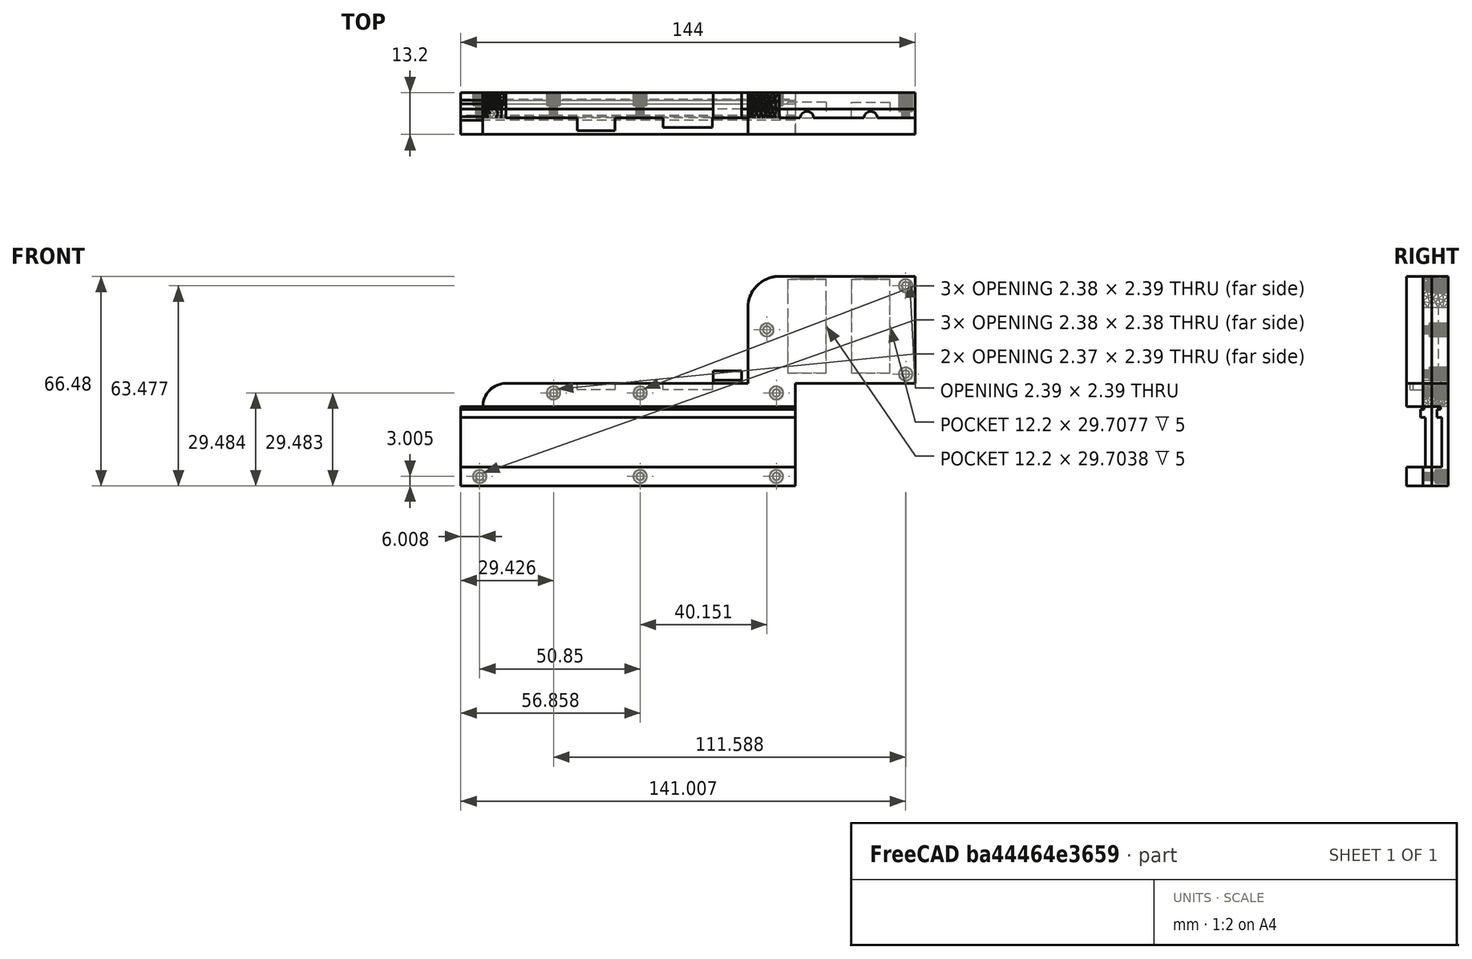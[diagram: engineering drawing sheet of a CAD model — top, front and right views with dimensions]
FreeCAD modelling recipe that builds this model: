
FCSTD DOCUMENT  (FreeCAD 0.19R24276 (Git))
Label: Feeder
License: All rights reserved
LicenseURL: http://en.wikipedia.org/wiki/All_rights_reserved
objects: Sketcher::SketchObject×7, Part::Feature×5, PartDesign::Pocket×3, Mesh::Feature×3, Part::Refine×2, PartDesign::Pad×1, PartDesign::Body×1
note: 23 computed .brp shape members not serialized (recipe doc carries the construction recipe); baked Part::Feature solids carry a one-line shape summary decoded from their .brp

FEATURE [Part::Feature] Feeder_8mm_Left_8mm_0_9_mm_tape001001_solid  label="Feeder_8mm_Left_8mm_0_9_mm_tape (Solid)"
  shape: bbox 144 x 12 x 66.48 mm, 7646 faces (baked)
FEATURE [Sketcher::SketchObject] Sketch  label="RightMain"
  FullyConstrained = false
  MapMode = 5
  Placement = pos=(0,0,0) rot=(1,0,0;1.5708rad)
  Support = -> [XZ_Plane]
  sketch-geometry (11):
    g0: LineSegment StartX=91 StartY=31.78 StartZ=0 EndX=91 EndY=7.78 EndZ=0
    g1: LineSegment StartX=144 StartY=41.78 StartZ=0 EndX=101 EndY=41.78 EndZ=0
    g2: LineSegment StartX=144 StartY=7.78 StartZ=0 EndX=144 EndY=41.78 EndZ=0
    g3: LineSegment StartX=106 StartY=7.78 StartZ=0 EndX=144 EndY=7.78 EndZ=0
    g4: LineSegment StartX=106 StartY=-24.7 StartZ=0 EndX=106 EndY=7.78 EndZ=0
    g5: LineSegment StartX=0 StartY=-24.7 StartZ=0 EndX=106 EndY=-24.7 EndZ=0
    g6: LineSegment StartX=0 StartY=0.4 StartZ=0 EndX=0 EndY=-24.7 EndZ=0
    g7: LineSegment StartX=7 StartY=0.4 StartZ=0 EndX=0 EndY=0.4 EndZ=0
    g8: LineSegment StartX=91 StartY=7.78 StartZ=0 EndX=14.38 EndY=7.78 EndZ=0
    g9: ArcOfCircle CenterX=14.401 CenterY=0.379003 CenterZ=0 NormalX=0 NormalY=0 NormalZ=1 AngleXU=0 Radius=7.40103 StartAngle=1.57363 EndAngle=3.13876
    g10: ArcOfCircle CenterX=101.048 CenterY=31.7317 CenterZ=0 NormalX=0 NormalY=0 NormalZ=1 AngleXU=0 Radius=10.0484 StartAngle=1.5756 EndAngle=3.13679
  constraints (23):
    c: Coincident(g1,g2)
    c: Vertical(g2)
    c: Coincident(g2,g3)
    c: Horizontal(g3)
    c: Coincident(g3,g4)
    c: Vertical(g4)
    c: Coincident(g4,g5)
    c: Horizontal(g5)
    c: Coincident(g5,g6)
    c: Coincident(g6,g7)
    c: Block(g8)
    c: Horizontal(g9,g8)
    c: Vertical(g9,g8)
    c: Block(g7)
    c: Horizontal(g9,g7)
    c: Vertical(g9,g7)
    c: Block(g1)
    c: Vertical(g10,g1)
    c: Horizontal(g10,g1)
    c: Block(g0)
    c: Horizontal(g0,g10)
    c: Vertical(g10,g0)
    c: DistanceX(g7,g7) = 7
FEATURE [Sketcher::SketchObject] Sketch001
  FullyConstrained = false
  Placement = pos=(0,0,0) rot=(1,0,0;1.5708rad)
  sketch-geometry (12):
    g0: LineSegment StartX=-41.78 StartY=5.2 StartZ=0 EndX=24.7 EndY=5.2 EndZ=0
    g1: LineSegment StartX=-41.78 StartY=-2.8 StartZ=0 EndX=-41.78 EndY=5.2 EndZ=0
    g2: LineSegment StartX=-0.4 StartY=-2.8 StartZ=0 EndX=-41.78 EndY=-2.8 EndZ=0
    g3: LineSegment StartX=-0.4 StartY=2.8 StartZ=0 EndX=-0.4 EndY=-2.8 EndZ=0
    g4: LineSegment StartX=0.5 StartY=2.8 StartZ=0 EndX=-0.4 EndY=2.8 EndZ=0
    g5: LineSegment StartX=0.5 StartY=1.7 StartZ=0 EndX=0.5 EndY=2.8 EndZ=0
    g6: LineSegment StartX=3 StartY=1.7 StartZ=0 EndX=0.5 EndY=1.7 EndZ=0
    g7: LineSegment StartX=3 StartY=3.2 StartZ=0 EndX=3 EndY=1.7 EndZ=0
    g8: LineSegment StartX=18.7 StartY=3.2 StartZ=0 EndX=3 EndY=3.2 EndZ=0
    g9: LineSegment StartX=18.7 StartY=-2.8 StartZ=0 EndX=18.7 EndY=3.2 EndZ=0
    g10: LineSegment StartX=24.7 StartY=-2.8 StartZ=0 EndX=18.7 EndY=-2.8 EndZ=0
    g11: LineSegment StartX=24.7 StartY=5.2 StartZ=0 EndX=24.7 EndY=-2.8 EndZ=0
  constraints (25):
    c: Horizontal(g0)
    c: Coincident(g0,g1)
    c: Vertical(g1)
    c: Coincident(g1,g2)
    c: Horizontal(g2)
    c: Coincident(g2,g3)
    c: Vertical(g3)
    c: Coincident(g3,g4)
    c: Horizontal(g4)
    c: Coincident(g4,g5)
    c: Vertical(g5)
    c: Coincident(g5,g6)
    c: Horizontal(g6)
    c: Coincident(g6,g7)
    c: Vertical(g7)
    c: Coincident(g7,g8)
    c: Horizontal(g8)
    c: Coincident(g8,g9)
    c: Vertical(g9)
    c: Coincident(g9,g10)
    c: Horizontal(g10)
    c: Coincident(g10,g11)
    c: Vertical(g11)
    c: Coincident(g11,g0)
    c: Block(g3)
FEATURE [PartDesign::Pad] Pad
  Direction = (1,1,1)
  Length = 8
  Length2 = 100
  Placement = pos=(0,0,0) rot=(1,0,0;1.5708rad)
  Profile = -> Sketch
  Type = 0
FEATURE [Sketcher::SketchObject] Sketch002  label="RightTapeHole"
  ExternalGeometry = -> [Pad]
  FullyConstrained = true
  MapMode = 5
  Placement = pos=(0,-8,-1.8e-15) rot=(1,0,0;1.5708rad)
  Support = -> [Pad]
  sketch-geometry (4):
    g0: LineSegment StartX=0 StartY=0.4 StartZ=0 EndX=106 EndY=0.4 EndZ=0
    g1: LineSegment StartX=106 StartY=0.4 StartZ=0 EndX=106 EndY=-0.5 EndZ=0
    g2: LineSegment StartX=106 StartY=-0.5 StartZ=0 EndX=0 EndY=-0.5 EndZ=0
    g3: LineSegment StartX=0 StartY=-0.5 StartZ=0 EndX=0 EndY=0.4 EndZ=0
  constraints (12):
    c: Coincident(g0,g1)
    c: Coincident(g1,g2)
    c: Coincident(g2,g3)
    c: Coincident(g3,g0)
    c: Horizontal(g0)
    c: Horizontal(g2)
    c: Vertical(g1)
    c: Vertical(g3)
    c: Horizontal(g-3,g0)
    c: Vertical(g0,g-3)
    c: Vertical(g0,g-4)
    c: DistanceY(g1,g1) = 0.9
FEATURE [PartDesign::Pocket] Pocket
  BaseFeature = -> Pad
  Length = 5.6
  Length2 = 100
  Placement = pos=(0,0,0) rot=(1,0,0;1.5708rad)
  Profile = -> Sketch002
  Type = 0
FEATURE [Sketcher::SketchObject] Sketch003  label="RightComponentHole1"
  ExternalGeometry = -> [Sketch]
  FullyConstrained = false
  MapMode = 5
  Placement = pos=(0,-8,-1.8e-15) rot=(1,0,0;1.5708rad)
  Support = -> [Pocket]
  sketch-geometry (4):
    g0: LineSegment StartX=0 StartY=0.4 StartZ=0 EndX=106 EndY=0.4 EndZ=0
    g1: LineSegment StartX=106 StartY=0.4 StartZ=0 EndX=106 EndY=-18.7 EndZ=0
    g2: LineSegment StartX=106 StartY=-18.7 StartZ=0 EndX=0 EndY=-18.7 EndZ=0
    g3: LineSegment StartX=0 StartY=-18.7 StartZ=0 EndX=0 EndY=0.4 EndZ=0
  constraints (11):
    c: Coincident(g0,g1)
    c: Coincident(g1,g2)
    c: Coincident(g2,g3)
    c: Coincident(g3,g0)
    c: Horizontal(g0)
    c: Horizontal(g2)
    c: Vertical(g3)
    c: Vertical(g0,g-3)
    c: DistanceY(g-5,g2) = 6
    c: Vertical(g1,g-5)
    c: Vertical(g0,g-4)
FEATURE [PartDesign::Pocket] Pocket001
  BaseFeature = -> Pocket
  Length = 4.5
  Length2 = 100
  Placement = pos=(0,0,0) rot=(1,0,0;1.5708rad)
  Profile = -> Sketch003
  Type = 0
FEATURE [Sketcher::SketchObject] Sketch004  label="RightComponentHole2"
  ExternalGeometry = -> [Sketch]
  FullyConstrained = true
  MapMode = 5
  Placement = pos=(0,-8,-1.8e-15) rot=(1,0,0;1.5708rad)
  Support = -> [Pad]
  sketch-geometry (4):
    g0: LineSegment StartX=0 StartY=-3 StartZ=0 EndX=106 EndY=-3 EndZ=0
    g1: LineSegment StartX=106 StartY=-3 StartZ=0 EndX=106 EndY=-18.7 EndZ=0
    g2: LineSegment StartX=106 StartY=-18.7 StartZ=0 EndX=0 EndY=-18.7 EndZ=0
    g3: LineSegment StartX=0 StartY=-18.7 StartZ=0 EndX=0 EndY=-3 EndZ=0
  constraints (12):
    c: Coincident(g0,g1)
    c: Coincident(g1,g2)
    c: Coincident(g2,g3)
    c: Coincident(g3,g0)
    c: Horizontal(g0)
    c: Horizontal(g2)
    c: Vertical(g1)
    c: Vertical(g3)
    c: Vertical(g2,g-3)
    c: Vertical(g1,g-3)
    c: DistanceY(g-3,g2) = 6
    c: DistanceY(g1,g0) = 15.7
FEATURE [PartDesign::Pocket] Pocket002
  BaseFeature = -> Pocket001
  Length = 6
  Length2 = 100
  Placement = pos=(0,0,0) rot=(1,0,0;1.5708rad)
  Profile = -> Sketch004
  Type = 0
FEATURE [PartDesign::Body] Body  label="Right"
  Group = -> [Sketch,Pad,Sketch002,Pocket,Sketch003,Pocket001,Sketch004,Pocket002]
  Origin = -> Origin
  Tip = -> Pocket002
FEATURE [Mesh::Feature] Powerful_Habbi  label="Powerful Habbi"
FEATURE [Part::Feature] Powerful_Habbi001
  shape: bbox 144 x 184.6 x 0.998 mm, 2680 faces, 0 solids (baked)
FEATURE [Part::Refine] Powerful_Habbi001001
  Source = -> Powerful_Habbi001
FEATURE [Part::Feature] Powerful_Habbi001001_cs
  shape: bbox 144 x 184.6 x 3e-07 mm, 0 faces, 0 solids (baked)
FEATURE [Sketcher::SketchObject] Sketch005
  FullyConstrained = false
  sketch-geometry (680):
    g0: LineSegment StartX=22.2578 StartY=-60.143 StartZ=0 EndX=22.1548 EndY=-59.743 EndZ=0
    g1: LineSegment StartX=22.1548 StartY=-59.743 StartZ=0 EndX=22.1233 EndY=-59.3596 EndZ=0
    g2: LineSegment StartX=22.1233 StartY=-59.3596 StartZ=0 EndX=22.0564 EndY=-58.5447 EndZ=0
    g3: LineSegment StartX=22.0564 StartY=-58.5447 StartZ=0 EndX=22 EndY=-58 EndZ=0
    g4: LineSegment StartX=22 StartY=-58 StartZ=0 EndX=22 EndY=-34 EndZ=0
    g5: LineSegment StartX=22 StartY=-34 StartZ=0 EndX=-54.63 EndY=-34 EndZ=0
    g6: LineSegment StartX=-54.63 StartY=-34 StartZ=0 EndX=-54.9663 EndY=-33.961 EndZ=0
    g7: LineSegment StartX=-54.9663 StartY=-33.961 StartZ=0 EndX=-55.7971 EndY=-33.8647 EndZ=0
    g8: LineSegment StartX=-55.7971 StartY=-33.8647 StartZ=0 EndX=-56.2377 EndY=-33.819 EndZ=0
    g9: LineSegment StartX=-56.2377 StartY=-33.819 StartZ=0 EndX=-56.4406 EndY=-33.7668 EndZ=0
    g10: LineSegment StartX=-56.4406 StartY=-33.7668 StartZ=0 EndX=-56.7481 EndY=-33.672 EndZ=0
    g11: LineSegment StartX=-56.7481 StartY=-33.672 StartZ=0 EndX=-57.3903 EndY=-33.4551 EndZ=0
    g12: LineSegment StartX=-57.3903 StartY=-33.4551 StartZ=0 EndX=-58.0429 EndY=-33.1436 EndZ=0
    g13: LineSegment StartX=-58.0429 StartY=-33.1436 StartZ=0 EndX=-58.6946 EndY=-32.7636 EndZ=0
    g14: LineSegment StartX=-58.6946 StartY=-32.7636 StartZ=0 EndX=-58.8229 EndY=-32.6707 EndZ=0
    g15: LineSegment StartX=-58.8229 StartY=-32.6707 StartZ=0 EndX=-59.2096 EndY=-32.3907 EndZ=0
    g16: LineSegment StartX=-59.2096 StartY=-32.3907 StartZ=0 EndX=-59.2288 EndY=-32.3737 EndZ=0
    g17: LineSegment StartX=-59.2288 StartY=-32.3737 StartZ=0 EndX=-59.7492 EndY=-31.9116 EndZ=0
    g18: LineSegment StartX=-59.7492 StartY=-31.9116 StartZ=0 EndX=-60.1883 EndY=-31.4563 EndZ=0
    g19: LineSegment StartX=-60.1883 StartY=-31.4563 StartZ=0 EndX=-60.1907 EndY=-31.4533 EndZ=0
    g20: LineSegment StartX=-60.1907 StartY=-31.4533 StartZ=0 EndX=-60.5844 EndY=-30.9498 EndZ=0
    g21: LineSegment StartX=-60.5844 StartY=-30.9498 StartZ=0 EndX=-60.611 EndY=-30.9105 EndZ=0
    g22: LineSegment StartX=-60.611 StartY=-30.9105 StartZ=0 EndX=-60.9365 EndY=-30.4302 EndZ=0
    g23: LineSegment StartX=-60.9365 StartY=-30.4302 StartZ=0 EndX=-61.213 EndY=-29.9119 EndZ=0
    g24: LineSegment StartX=-61.213 StartY=-29.9119 StartZ=0 EndX=-61.2418 EndY=-29.8501 EndZ=0
    g25: LineSegment StartX=-61.2418 StartY=-29.8501 StartZ=0 EndX=-61.4535 EndY=-29.3965 EndZ=0
    g26: LineSegment StartX=-61.4535 StartY=-29.3965 StartZ=0 EndX=-61.6287 EndY=-28.8855 EndZ=0
    g27: LineSegment StartX=-61.6287 StartY=-28.8855 StartZ=0 EndX=-61.7232 EndY=-28.6099 EndZ=0
    g28: LineSegment StartX=-61.7232 StartY=-28.6099 StartZ=0 EndX=-61.7741 EndY=-28.429 EndZ=0
    g29: LineSegment StartX=-61.7741 StartY=-28.429 StartZ=0 EndX=-61.8609 EndY=-27.994 EndZ=0
    g30: LineSegment StartX=-61.8609 StartY=-27.994 StartZ=0 EndX=-61.932 EndY=-27.62 EndZ=0
    g31: LineSegment StartX=-61.932 StartY=-27.62 StartZ=0 EndX=-69 EndY=-27.62 EndZ=0
    g32: LineSegment StartX=-69 StartY=-27.62 StartZ=0 EndX=-69 EndY=-1.52 EndZ=0
    g33: LineSegment StartX=-69 StartY=-1.52 StartZ=0 EndX=-44 EndY=-1.52 EndZ=0
    g34: LineSegment StartX=-44 StartY=-1.52 StartZ=0 EndX=-44 EndY=5.98 EndZ=0
    g35: LineSegment StartX=-44 StartY=5.98 StartZ=0 EndX=-49 EndY=5.98 EndZ=0
    g36: LineSegment StartX=-49 StartY=5.98 StartZ=0 EndX=-49 EndY=10.98 EndZ=0
    g37: LineSegment StartX=-49 StartY=10.98 StartZ=0 EndX=-38 EndY=10.98 EndZ=0
    g38: LineSegment StartX=-38 StartY=10.98 StartZ=0 EndX=-38 EndY=-1.52 EndZ=0
    g39: LineSegment StartX=-38 StartY=-1.52 StartZ=0 EndX=16 EndY=-1.52 EndZ=0
    g40: LineSegment StartX=16 StartY=-1.52 StartZ=0 EndX=16 EndY=5.98 EndZ=0
    g41: LineSegment StartX=16 StartY=5.98 StartZ=0 EndX=11 EndY=5.98 EndZ=0
    g42: LineSegment StartX=11 StartY=5.98 StartZ=0 EndX=11 EndY=10.98 EndZ=0
    g43: LineSegment StartX=11 StartY=10.98 StartZ=0 EndX=22 EndY=10.98 EndZ=0
    g44: LineSegment StartX=22 StartY=10.98 StartZ=0 EndX=22 EndY=109.74 EndZ=0
    g45: LineSegment StartX=22 StartY=109.74 StartZ=0 EndX=22.0004 EndY=109.745 EndZ=0
    g46: LineSegment StartX=22.0004 StartY=109.745 StartZ=0 EndX=22.0438 EndY=110.287 EndZ=0
    g47: LineSegment StartX=22.0438 StartY=110.287 StartZ=0 EndX=22.0765 EndY=110.747 EndZ=0
    g48: LineSegment StartX=22.0765 StartY=110.747 StartZ=0 EndX=22.1579 EndY=111.153 EndZ=0
    g49: LineSegment StartX=22.1579 StartY=111.153 StartZ=0 EndX=22.1657 EndY=111.191 EndZ=0
    g50: LineSegment StartX=22.1657 StartY=111.191 StartZ=0 EndX=22.3059 EndY=111.744 EndZ=0
    g51: LineSegment StartX=22.3059 StartY=111.744 StartZ=0 EndX=22.3433 EndY=111.852 EndZ=0
    g52: LineSegment StartX=22.3433 StartY=111.852 StartZ=0 EndX=22.4628 EndY=112.196 EndZ=0
    g53: LineSegment StartX=22.4628 StartY=112.196 StartZ=0 EndX=22.5072 EndY=112.293 EndZ=0
    g54: LineSegment StartX=22.5072 StartY=112.293 StartZ=0 EndX=22.7647 EndY=112.857 EndZ=0
    g55: LineSegment StartX=22.7647 StartY=112.857 StartZ=0 EndX=22.9938 EndY=113.277 EndZ=0
    g56: LineSegment StartX=22.9938 StartY=113.277 StartZ=0 EndX=23.087 EndY=113.409 EndZ=0
    g57: LineSegment StartX=23.087 StartY=113.409 StartZ=0 EndX=23.4483 EndY=113.924 EndZ=0
    g58: LineSegment StartX=23.4483 StartY=113.924 StartZ=0 EndX=23.7598 EndY=114.304 EndZ=0
    g59: LineSegment StartX=23.7598 StartY=114.304 StartZ=0 EndX=23.8929 EndY=114.435 EndZ=0
    g60: LineSegment StartX=23.8929 StartY=114.435 StartZ=0 EndX=24.3275 EndY=114.862 EndZ=0
    g61: LineSegment StartX=24.3275 StartY=114.862 StartZ=0 EndX=24.6084 EndY=115.096 EndZ=0
    g62: LineSegment StartX=24.6084 StartY=115.096 StartZ=0 EndX=25.1034 EndY=115.407 EndZ=0
    g63: LineSegment StartX=25.1034 StartY=115.407 StartZ=0 EndX=25.5769 EndY=115.732 EndZ=0
    g64: LineSegment StartX=25.5769 StartY=115.732 StartZ=0 EndX=25.6013 EndY=115.749 EndZ=0
    g65: LineSegment StartX=25.6013 StartY=115.749 StartZ=0 EndX=26.0166 EndY=115.924 EndZ=0
    g66: LineSegment StartX=26.0166 StartY=115.924 StartZ=0 EndX=26.0247 EndY=115.927 EndZ=0
    g67: LineSegment StartX=26.0247 StartY=115.927 StartZ=0 EndX=26.8368 EndY=116.259 EndZ=0
    g68: LineSegment StartX=26.8368 StartY=116.259 StartZ=0 EndX=26.8415 EndY=116.26 EndZ=0
    g69: LineSegment StartX=26.8415 StartY=116.26 StartZ=0 EndX=27.5233 EndY=116.413 EndZ=0
    g70: LineSegment StartX=27.5233 StartY=116.413 StartZ=0 EndX=28.1555 EndY=116.518 EndZ=0
    g71: LineSegment StartX=28.1555 StartY=116.518 StartZ=0 EndX=28.2469 EndY=116.533 EndZ=0
    g72: LineSegment StartX=28.2469 StartY=116.533 StartZ=0 EndX=28.2972 EndY=116.534 EndZ=0
    g73: LineSegment StartX=28.2972 StartY=116.534 StartZ=0 EndX=28.6445 EndY=116.543 EndZ=0
    g74: LineSegment StartX=28.6445 StartY=116.543 StartZ=0 EndX=29.0398 EndY=116.558 EndZ=0
    g75: LineSegment StartX=29.0398 StartY=116.558 StartZ=0 EndX=29.4145 EndY=116.555 EndZ=0
    g76: LineSegment StartX=29.4145 StartY=116.555 StartZ=0 EndX=29.6463 EndY=116.551 EndZ=0
    g77: LineSegment StartX=29.6463 StartY=116.551 StartZ=0 EndX=30.2252 EndY=116.551 EndZ=0
    g78: LineSegment StartX=30.2252 StartY=116.551 StartZ=0 EndX=30.8464 EndY=116.513 EndZ=0
    g79: LineSegment StartX=30.8464 StartY=116.513 StartZ=0 EndX=31.0094 EndY=116.503 EndZ=0
    g80: LineSegment StartX=31.0094 StartY=116.503 StartZ=0 EndX=31.1374 EndY=116.49 EndZ=0
    g81: LineSegment StartX=31.1374 StartY=116.49 StartZ=0 EndX=31.9969 EndY=116.297 EndZ=0
    g82: LineSegment StartX=31.9969 StartY=116.297 StartZ=0 EndX=32.1482 EndY=116.266 EndZ=0
    g83: LineSegment StartX=32.1482 StartY=116.266 StartZ=0 EndX=32.6265 EndY=116.085 EndZ=0
    g84: LineSegment StartX=32.6265 StartY=116.085 StartZ=0 EndX=33.0541 EndY=115.919 EndZ=0
    g85: LineSegment StartX=33.0541 StartY=115.919 StartZ=0 EndX=33.3653 EndY=115.763 EndZ=0
    g86: LineSegment StartX=33.3653 StartY=115.763 StartZ=0 EndX=33.4998 EndY=115.695 EndZ=0
    g87: LineSegment StartX=33.4998 StartY=115.695 StartZ=0 EndX=33.5829 EndY=115.642 EndZ=0
    g88: LineSegment StartX=33.5829 StartY=115.642 StartZ=0 EndX=34.0056 EndY=115.373 EndZ=0
    g89: LineSegment StartX=34.0056 StartY=115.373 StartZ=0 EndX=34.4724 EndY=115.03 EndZ=0
    g90: LineSegment StartX=34.4724 StartY=115.03 StartZ=0 EndX=34.935 EndY=114.613 EndZ=0
    g91: LineSegment StartX=34.935 StartY=114.613 StartZ=0 EndX=35.0086 EndY=114.547 EndZ=0
    g92: LineSegment StartX=35.0086 StartY=114.547 StartZ=0 EndX=35.3629 EndY=114.156 EndZ=0
    g93: LineSegment StartX=35.3629 StartY=114.156 StartZ=0 EndX=35.7691 EndY=113.62 EndZ=0
    g94: LineSegment StartX=35.7691 StartY=113.62 StartZ=0 EndX=35.8815 EndY=113.471 EndZ=0
    g95: LineSegment StartX=35.8815 StartY=113.471 StartZ=0 EndX=36.1773 EndY=112.962 EndZ=0
    g96: LineSegment StartX=36.1773 StartY=112.962 StartZ=0 EndX=36.4572 EndY=112.391 EndZ=0
    g97: LineSegment StartX=36.4572 StartY=112.391 StartZ=0 EndX=36.4701 EndY=112.365 EndZ=0
    g98: LineSegment StartX=36.4701 StartY=112.365 StartZ=0 EndX=36.5839 EndY=112.08 EndZ=0
    g99: LineSegment StartX=36.5839 StartY=112.08 StartZ=0 EndX=36.699 EndY=111.654 EndZ=0
    g100: LineSegment StartX=36.699 StartY=111.654 StartZ=0 EndX=36.8721 EndY=111.013 EndZ=0
    g101: LineSegment StartX=36.8721 StartY=111.013 StartZ=0 EndX=36.9067 EndY=110.864 EndZ=0
    g102: LineSegment StartX=36.9067 StartY=110.864 StartZ=0 EndX=36.9178 EndY=110.728 EndZ=0
    g103: LineSegment StartX=36.9178 StartY=110.728 StartZ=0 EndX=36.9647 EndY=110.165 EndZ=0
    g104: LineSegment StartX=36.9647 StartY=110.165 StartZ=0 EndX=37 EndY=109.74 EndZ=0
    g105: LineSegment StartX=37 StartY=109.74 StartZ=0 EndX=37 EndY=-34 EndZ=0
    g106: LineSegment StartX=37 StartY=-34 StartZ=0 EndX=75 EndY=-34 EndZ=0
    g107: LineSegment StartX=75 StartY=-34 StartZ=0 EndX=75 EndY=-68 EndZ=0
    g108: LineSegment StartX=75 StartY=-68 StartZ=0 EndX=32 EndY=-68 EndZ=0
    g109: LineSegment StartX=32 StartY=-68 StartZ=0 EndX=31.1549 EndY=-67.9109 EndZ=0
    g110: LineSegment StartX=31.1549 StartY=-67.9109 StartZ=0 EndX=30.114 EndY=-67.8011 EndZ=0
    g111: LineSegment StartX=30.114 StartY=-67.8011 StartZ=0 EndX=30.0246 EndY=-67.8001 EndZ=0
    g112: LineSegment StartX=30.0246 StartY=-67.8001 StartZ=0 EndX=29.5979 EndY=-67.6916 EndZ=0
    g113: LineSegment StartX=29.5979 StartY=-67.6916 StartZ=0 EndX=28.6289 EndY=-67.3787 EndZ=0
    g114: LineSegment StartX=28.6289 StartY=-67.3787 StartZ=0 EndX=28.1683 EndY=-67.23 EndZ=0
    g115: LineSegment StartX=28.1683 StartY=-67.23 StartZ=0 EndX=27.6703 EndY=-66.9991 EndZ=0
    g116: LineSegment StartX=27.6703 StartY=-66.9991 StartZ=0 EndX=26.7851 EndY=-66.4961 EndZ=0
    g117: LineSegment StartX=26.7851 StartY=-66.4961 StartZ=0 EndX=26.4215 EndY=-66.2895 EndZ=0
    g118: LineSegment StartX=26.4215 StartY=-66.2895 StartZ=0 EndX=25.9346 EndY=-65.9344 EndZ=0
    g119: LineSegment StartX=25.9346 StartY=-65.9344 StartZ=0 EndX=25.1287 EndY=-65.2168 EndZ=0
    g120: LineSegment StartX=25.1287 StartY=-65.2168 StartZ=0 EndX=24.8183 EndY=-64.9405 EndZ=0
    g121: LineSegment StartX=24.8183 StartY=-64.9405 StartZ=0 EndX=24.3908 EndY=-64.4727 EndZ=0
    g122: LineSegment StartX=24.3908 StartY=-64.4727 StartZ=0 EndX=24.1519 EndY=-64.1434 EndZ=0
    g123: LineSegment StartX=24.1519 StartY=-64.1434 StartZ=0 EndX=23.5226 EndY=-63.2762 EndZ=0
    g124: LineSegment StartX=23.5226 StartY=-63.2762 StartZ=0 EndX=23.1957 EndY=-62.7231 EndZ=0
    g125: LineSegment StartX=23.1957 StartY=-62.7231 StartZ=0 EndX=22.822 EndY=-61.9087 EndZ=0
    g126: LineSegment StartX=22.822 StartY=-61.9087 StartZ=0 EndX=22.6746 EndY=-61.5878 EndZ=0
    g127: LineSegment StartX=22.6746 StartY=-61.5878 StartZ=0 EndX=22.4769 EndY=-60.9933 EndZ=0
    g128: LineSegment StartX=22.4769 StartY=-60.9933 StartZ=0 EndX=22.2578 EndY=-60.143 EndZ=0
    g129: LineSegment StartX=29.2243 StartY=-31.2822 StartZ=0 EndX=29.3015 EndY=-31.55 EndZ=0
    g130: LineSegment StartX=29.3015 StartY=-31.55 StartZ=0 EndX=29.36 EndY=-31.7295 EndZ=0
    g131: LineSegment StartX=29.36 StartY=-31.7295 StartZ=0 EndX=29.4543 EndY=-31.8935 EndZ=0
    g132: LineSegment StartX=29.4543 StartY=-31.8935 StartZ=0 EndX=29.5983 EndY=-32.1254 EndZ=0
    g133: LineSegment StartX=29.5983 StartY=-32.1254 StartZ=0 EndX=29.7952 EndY=-32.3164 EndZ=0
    g134: LineSegment StartX=29.7952 StartY=-32.3164 StartZ=0 EndX=29.8738 EndY=-32.3802 EndZ=0
    g135: LineSegment StartX=29.8738 StartY=-32.3802 StartZ=0 EndX=29.9861 EndY=-32.4753 EndZ=0
    g136: LineSegment StartX=29.9861 StartY=-32.4753 StartZ=0 EndX=30.1143 EndY=-32.5496 EndZ=0
    g137: LineSegment StartX=30.1143 StartY=-32.5496 StartZ=0 EndX=30.3544 EndY=-32.6775 EndZ=0
    g138: LineSegment StartX=30.3544 StartY=-32.6775 StartZ=0 EndX=30.5398 EndY=-32.7174 EndZ=0
    g139: LineSegment StartX=30.5398 StartY=-32.7174 StartZ=0 EndX=30.8232 EndY=-32.7915 EndZ=0
    g140: LineSegment StartX=30.8232 StartY=-32.7915 StartZ=0 EndX=30.9217 EndY=-32.7893 EndZ=0
    g141: LineSegment StartX=30.9217 StartY=-32.7893 StartZ=0 EndX=31.1119 EndY=-32.7724 EndZ=0
    g142: LineSegment StartX=31.1119 StartY=-32.7724 StartZ=0 EndX=31.4781 EndY=-32.7334 EndZ=0
    g143: LineSegment StartX=31.4781 StartY=-32.7334 StartZ=0 EndX=31.6639 EndY=-32.6696 EndZ=0
    g144: LineSegment StartX=31.6639 StartY=-32.6696 StartZ=0 EndX=31.8837 EndY=-32.5526 EndZ=0
    g145: LineSegment StartX=31.8837 StartY=-32.5526 StartZ=0 EndX=32.0689 EndY=-32.443 EndZ=0
    g146: LineSegment StartX=32.0689 StartY=-32.443 StartZ=0 EndX=32.3073 EndY=-32.188 EndZ=0
    g147: LineSegment StartX=32.3073 StartY=-32.188 StartZ=0 EndX=32.4701 EndY=-32.0261 EndZ=0
    g148: LineSegment StartX=32.4701 StartY=-32.0261 StartZ=0 EndX=32.5377 EndY=-31.9 EndZ=0
    g149: LineSegment StartX=32.5377 StartY=-31.9 StartZ=0 EndX=32.7076 EndY=-31.5631 EndZ=0
    g150: LineSegment StartX=32.7076 StartY=-31.5631 StartZ=0 EndX=32.7627 EndY=-30.7951 EndZ=0
    g151: LineSegment StartX=32.7627 StartY=-30.7951 StartZ=0 EndX=32.7686 EndY=-30.7044 EndZ=0
    g152: LineSegment StartX=32.7686 StartY=-30.7044 StartZ=0 EndX=32.7706 EndY=-30.6847 EndZ=0
    g153: LineSegment StartX=32.7706 StartY=-30.6847 StartZ=0 EndX=32.7462 EndY=-30.6014 EndZ=0
    g154: LineSegment StartX=32.7462 StartY=-30.6014 StartZ=0 EndX=32.6332 EndY=-30.2562 EndZ=0
    g155: LineSegment StartX=32.6332 StartY=-30.2562 StartZ=0 EndX=32.4764 EndY=-30.0236 EndZ=0
    g156: LineSegment StartX=32.4764 StartY=-30.0236 StartZ=0 EndX=32.3143 EndY=-29.7771 EndZ=0
    g157: LineSegment StartX=32.3143 StartY=-29.7771 StartZ=0 EndX=32.1555 EndY=-29.6399 EndZ=0
    g158: LineSegment StartX=32.1555 StartY=-29.6399 StartZ=0 EndX=31.8604 EndY=-29.4347 EndZ=0
    g159: LineSegment StartX=31.8604 StartY=-29.4347 StartZ=0 EndX=31.7716 EndY=-29.392 EndZ=0
    g160: LineSegment StartX=31.7716 StartY=-29.392 StartZ=0 EndX=31.6401 EndY=-29.3275 EndZ=0
    g161: LineSegment StartX=31.6401 StartY=-29.3275 StartZ=0 EndX=31.4953 EndY=-29.2849 EndZ=0
    g162: LineSegment StartX=31.4953 StartY=-29.2849 StartZ=0 EndX=31.1449 EndY=-29.2193 EndZ=0
    g163: LineSegment StartX=31.1449 StartY=-29.2193 StartZ=0 EndX=30.958 EndY=-29.2049 EndZ=0
    g164: LineSegment StartX=30.958 StartY=-29.2049 StartZ=0 EndX=30.6019 EndY=-29.2889 EndZ=0
    g165: LineSegment StartX=30.6019 StartY=-29.2889 StartZ=0 EndX=30.3698 EndY=-29.3387 EndZ=0
    g166: LineSegment StartX=30.3698 StartY=-29.3387 StartZ=0 EndX=30.2773 EndY=-29.3609 EndZ=0
    g167: LineSegment StartX=30.2773 StartY=-29.3609 StartZ=0 EndX=30.234 EndY=-29.3759 EndZ=0
    g168: LineSegment StartX=30.234 StartY=-29.3759 StartZ=0 EndX=30.005 EndY=-29.5261 EndZ=0
    g169: LineSegment StartX=30.005 StartY=-29.5261 StartZ=0 EndX=29.8031 EndY=-29.6607 EndZ=0
    g170: LineSegment StartX=29.8031 StartY=-29.6607 StartZ=0 EndX=29.7071 EndY=-29.7588 EndZ=0
    g171: LineSegment StartX=29.7071 StartY=-29.7588 StartZ=0 EndX=29.4564 EndY=-30.0911 EndZ=0
    g172: LineSegment StartX=29.4564 StartY=-30.0911 StartZ=0 EndX=29.4316 EndY=-30.1266 EndZ=0
    g173: LineSegment StartX=29.4316 StartY=-30.1266 StartZ=0 EndX=29.3222 EndY=-30.4765 EndZ=0
    g174: LineSegment StartX=29.3222 StartY=-30.4765 StartZ=0 EndX=29.2358 EndY=-30.7356 EndZ=0
    g175: LineSegment StartX=29.2358 StartY=-30.7356 StartZ=0 EndX=29.213 EndY=-30.824 EndZ=0
    g176: LineSegment StartX=29.213 StartY=-30.824 StartZ=0 EndX=29.2134 EndY=-31.0143 EndZ=0
    g177: LineSegment StartX=29.2134 StartY=-31.0143 StartZ=0 EndX=29.2243 EndY=-31.2822 EndZ=0
    g178: LineSegment StartX=-10.9983 StartY=-3.14962 StartZ=0 EndX=-11.0539 EndY=-3.12454 EndZ=0
    g179: LineSegment StartX=-11.0539 StartY=-3.12454 StartZ=0 EndX=-11.3484 EndY=-2.95663 EndZ=0
    g180: LineSegment StartX=-11.3484 StartY=-2.95663 StartZ=0 EndX=-11.6072 EndY=-2.8042 EndZ=0
    g181: LineSegment StartX=-11.6072 StartY=-2.8042 StartZ=0 EndX=-11.7478 EndY=-2.77512 EndZ=0
    g182: LineSegment StartX=-11.7478 StartY=-2.77512 StartZ=0 EndX=-12.0821 EndY=-2.727 EndZ=0
    g183: LineSegment StartX=-12.0821 StartY=-2.727 StartZ=0 EndX=-12.1168 EndY=-2.72201 EndZ=0
    g184: LineSegment StartX=-12.1168 StartY=-2.72201 StartZ=0 EndX=-12.1452 EndY=-2.72276 EndZ=0
    g185: LineSegment StartX=-12.1452 StartY=-2.72276 StartZ=0 EndX=-12.269 EndY=-2.72603 EndZ=0
    g186: LineSegment StartX=-12.269 StartY=-2.72603 StartZ=0 EndX=-12.4173 EndY=-2.74162 EndZ=0
    g187: LineSegment StartX=-12.4173 StartY=-2.74162 StartZ=0 EndX=-12.7374 EndY=-2.83449 EndZ=0
    g188: LineSegment StartX=-12.7374 StartY=-2.83449 StartZ=0 EndX=-12.8939 EndY=-2.89078 EndZ=0
    g189: LineSegment StartX=-12.8939 StartY=-2.89078 StartZ=0 EndX=-13.0398 EndY=-2.97169 EndZ=0
    g190: LineSegment StartX=-13.0398 StartY=-2.97169 StartZ=0 EndX=-13.3067 EndY=-3.14146 EndZ=0
    g191: LineSegment StartX=-13.3067 StartY=-3.14146 StartZ=0 EndX=-13.4258 EndY=-3.25113 EndZ=0
    g192: LineSegment StartX=-13.4258 StartY=-3.25113 StartZ=0 EndX=-13.6191 EndY=-3.50109 EndZ=0
    g193: LineSegment StartX=-13.6191 StartY=-3.50109 StartZ=0 EndX=-13.71 EndY=-3.62839 EndZ=0
    g194: LineSegment StartX=-13.71 StartY=-3.62839 StartZ=0 EndX=-13.795 EndY=-3.86413 EndZ=0
    g195: LineSegment StartX=-13.795 StartY=-3.86413 StartZ=0 EndX=-13.9119 EndY=-4.15992 EndZ=0
    g196: LineSegment StartX=-13.9119 StartY=-4.15992 StartZ=0 EndX=-13.9309 EndY=-4.36405 EndZ=0
    g197: LineSegment StartX=-13.9309 StartY=-4.36405 StartZ=0 EndX=-13.9269 EndY=-4.72034 EndZ=0
    g198: LineSegment StartX=-13.9269 StartY=-4.72034 StartZ=0 EndX=-13.9043 EndY=-4.9154 EndZ=0
    g199: LineSegment StartX=-13.9043 StartY=-4.9154 StartZ=0 EndX=-13.841 EndY=-5.10331 EndZ=0
    g200: LineSegment StartX=-13.841 StartY=-5.10331 StartZ=0 EndX=-13.7485 EndY=-5.34626 EndZ=0
    g201: LineSegment StartX=-13.7485 StartY=-5.34626 StartZ=0 EndX=-13.7221 EndY=-5.3912 EndZ=0
    g202: LineSegment StartX=-13.7221 StartY=-5.3912 StartZ=0 EndX=-13.6442 EndY=-5.51393 EndZ=0
    g203: LineSegment StartX=-13.6442 StartY=-5.51393 StartZ=0 EndX=-13.3843 EndY=-5.82034 EndZ=0
    g204: LineSegment StartX=-13.3843 StartY=-5.82034 StartZ=0 EndX=-13.2674 EndY=-5.91061 EndZ=0
    g205: LineSegment StartX=-13.2674 StartY=-5.91061 StartZ=0 EndX=-12.915 EndY=-6.14519 EndZ=0
    g206: LineSegment StartX=-12.915 StartY=-6.14519 StartZ=0 EndX=-12.7816 EndY=-6.1981 EndZ=0
    g207: LineSegment StartX=-12.7816 StartY=-6.1981 StartZ=0 EndX=-12.5959 EndY=-6.26215 EndZ=0
    g208: LineSegment StartX=-12.5959 StartY=-6.26215 StartZ=0 EndX=-12.3105 EndY=-6.2964 EndZ=0
    g209: LineSegment StartX=-12.3105 StartY=-6.2964 StartZ=0 EndX=-12.0456 EndY=-6.31351 EndZ=0
    g210: LineSegment StartX=-12.0456 StartY=-6.31351 StartZ=0 EndX=-12.0455 EndY=-6.31352 EndZ=0
    g211: LineSegment StartX=-12.0455 StartY=-6.31352 StartZ=0 EndX=-12.0408 EndY=-6.31397 EndZ=0
    g212: LineSegment StartX=-12.0408 StartY=-6.31397 StartZ=0 EndX=-12.0339 EndY=-6.31346 EndZ=0
    g213: LineSegment StartX=-12.0339 StartY=-6.31346 StartZ=0 EndX=-12.0338 EndY=-6.31346 EndZ=0
    g214: LineSegment StartX=-12.0338 StartY=-6.31346 StartZ=0 EndX=-12.005 EndY=-6.30546 EndZ=0
    g215: LineSegment StartX=-12.005 StartY=-6.30546 StartZ=0 EndX=-11.5697 EndY=-6.20815 EndZ=0
    g216: LineSegment StartX=-11.5697 StartY=-6.20815 StartZ=0 EndX=-11.4193 EndY=-6.15324 EndZ=0
    g217: LineSegment StartX=-11.4193 StartY=-6.15324 StartZ=0 EndX=-11.2829 EndY=-6.07928 EndZ=0
    g218: LineSegment StartX=-11.2829 StartY=-6.07928 StartZ=0 EndX=-11.0228 EndY=-5.91868 EndZ=0
    g219: LineSegment StartX=-11.0228 StartY=-5.91868 StartZ=0 EndX=-10.8987 EndY=-5.78236 EndZ=0
    g220: LineSegment StartX=-10.8987 StartY=-5.78236 StartZ=0 EndX=-10.659 EndY=-5.51956 EndZ=0
    g221: LineSegment StartX=-10.659 StartY=-5.51956 StartZ=0 EndX=-10.5602 EndY=-5.35058 EndZ=0
    g222: LineSegment StartX=-10.5602 StartY=-5.35058 StartZ=0 EndX=-10.4119 EndY=-4.92552 EndZ=0
    g223: LineSegment StartX=-10.4119 StartY=-4.92552 StartZ=0 EndX=-10.3864 EndY=-4.86045 EndZ=0
    g224: LineSegment StartX=-10.3864 StartY=-4.86045 StartZ=0 EndX=-10.3784 EndY=-4.80026 EndZ=0
    g225: LineSegment StartX=-10.3784 StartY=-4.80026 StartZ=0 EndX=-10.3599 EndY=-4.60146 EndZ=0
    g226: LineSegment StartX=-10.3599 StartY=-4.60146 StartZ=0 EndX=-10.3833 EndY=-4.29881 EndZ=0
    g227: LineSegment StartX=-10.3833 StartY=-4.29881 StartZ=0 EndX=-10.4017 EndY=-4.16907 EndZ=0
    g228: LineSegment StartX=-10.4017 StartY=-4.16907 StartZ=0 EndX=-10.4369 EndY=-3.98977 EndZ=0
    g229: LineSegment StartX=-10.4369 StartY=-3.98977 StartZ=0 EndX=-10.4735 EndY=-3.93988 EndZ=0
    g230: LineSegment StartX=-10.4735 StartY=-3.93988 StartZ=0 EndX=-10.63 EndY=-3.56218 EndZ=0
    g231: LineSegment StartX=-10.63 StartY=-3.56218 StartZ=0 EndX=-10.8993 EndY=-3.23898 EndZ=0
    g232: LineSegment StartX=-10.8993 StartY=-3.23898 StartZ=0 EndX=-10.955 EndY=-3.1807 EndZ=0
    g233: LineSegment StartX=-10.955 StartY=-3.1807 StartZ=0 EndX=-10.9983 EndY=-3.14962 EndZ=0
    g234: LineSegment StartX=-12.6901 StartY=-32.7078 StartZ=0 EndX=-12.6721 EndY=-32.7085 EndZ=0
    g235: LineSegment StartX=-12.6721 StartY=-32.7085 StartZ=0 EndX=-12.6151 EndY=-32.7169 EndZ=0
    g236: LineSegment StartX=-12.6151 StartY=-32.7169 StartZ=0 EndX=-12.0807 EndY=-32.7959 EndZ=0
    g237: LineSegment StartX=-12.0807 StartY=-32.7959 StartZ=0 EndX=-12.0771 EndY=-32.7954 EndZ=0
    g238: LineSegment StartX=-12.0771 StartY=-32.7954 StartZ=0 EndX=-12.0595 EndY=-32.7928 EndZ=0
    g239: LineSegment StartX=-12.0595 StartY=-32.7928 StartZ=0 EndX=-11.7028 EndY=-32.7396 EndZ=0
    g240: LineSegment StartX=-11.7028 StartY=-32.7396 StartZ=0 EndX=-11.518 EndY=-32.6766 EndZ=0
    g241: LineSegment StartX=-11.518 StartY=-32.6766 StartZ=0 EndX=-11.1278 EndY=-32.4659 EndZ=0
    g242: LineSegment StartX=-11.1278 StartY=-32.4659 StartZ=0 EndX=-11.087 EndY=-32.4438 EndZ=0
    g243: LineSegment StartX=-11.087 StartY=-32.4438 StartZ=0 EndX=-10.9375 EndY=-32.3087 EndZ=0
    g244: LineSegment StartX=-10.9375 StartY=-32.3087 StartZ=0 EndX=-10.6571 EndY=-31.9726 EndZ=0
    g245: LineSegment StartX=-10.6571 StartY=-31.9726 StartZ=0 EndX=-10.5786 EndY=-31.8609 EndZ=0
    g246: LineSegment StartX=-10.5786 StartY=-31.8609 StartZ=0 EndX=-10.5502 EndY=-31.7829 EndZ=0
    g247: LineSegment StartX=-10.5502 StartY=-31.7829 StartZ=0 EndX=-10.3928 EndY=-31.3777 EndZ=0
    g248: LineSegment StartX=-10.3928 StartY=-31.3777 StartZ=0 EndX=-10.3727 EndY=-31.1916 EndZ=0
    g249: LineSegment StartX=-10.3727 StartY=-31.1916 StartZ=0 EndX=-10.3575 EndY=-31.013 EndZ=0
    g250: LineSegment StartX=-10.3575 StartY=-31.013 StartZ=0 EndX=-10.3543 EndY=-30.9758 EndZ=0
    g251: LineSegment StartX=-10.3543 StartY=-30.9758 StartZ=0 EndX=-10.3553 EndY=-30.9653 EndZ=0
    g252: LineSegment StartX=-10.3553 StartY=-30.9653 StartZ=0 EndX=-10.3688 EndY=-30.8296 EndZ=0
    g253: LineSegment StartX=-10.3688 StartY=-30.8296 StartZ=0 EndX=-10.3828 EndY=-30.7636 EndZ=0
    g254: LineSegment StartX=-10.3828 StartY=-30.7636 StartZ=0 EndX=-10.4518 EndY=-30.4385 EndZ=0
    g255: LineSegment StartX=-10.4518 StartY=-30.4385 StartZ=0 EndX=-10.467 EndY=-30.3683 EndZ=0
    g256: LineSegment StartX=-10.467 StartY=-30.3683 StartZ=0 EndX=-10.5062 EndY=-30.2965 EndZ=0
    g257: LineSegment StartX=-10.5062 StartY=-30.2965 StartZ=0 EndX=-10.5081 EndY=-30.2929 EndZ=0
    g258: LineSegment StartX=-10.5081 StartY=-30.2929 StartZ=0 EndX=-10.6243 EndY=-30.0687 EndZ=0
    g259: LineSegment StartX=-10.6243 StartY=-30.0687 StartZ=0 EndX=-10.8426 EndY=-29.7881 EndZ=0
    g260: LineSegment StartX=-10.8426 StartY=-29.7881 StartZ=0 EndX=-10.8947 EndY=-29.7181 EndZ=0
    g261: LineSegment StartX=-10.8947 StartY=-29.7181 StartZ=0 EndX=-11.042 EndY=-29.5994 EndZ=0
    g262: LineSegment StartX=-11.042 StartY=-29.5994 StartZ=0 EndX=-11.2563 EndY=-29.4416 EndZ=0
    g263: LineSegment StartX=-11.2563 StartY=-29.4416 StartZ=0 EndX=-11.5175 EndY=-29.3316 EndZ=0
    g264: LineSegment StartX=-11.5175 StartY=-29.3316 StartZ=0 EndX=-11.692 EndY=-29.265 EndZ=0
    g265: LineSegment StartX=-11.692 StartY=-29.265 StartZ=0 EndX=-11.977 EndY=-29.2305 EndZ=0
    g266: LineSegment StartX=-11.977 StartY=-29.2305 StartZ=0 EndX=-12.1594 EndY=-29.2063 EndZ=0
    g267: LineSegment StartX=-12.1594 StartY=-29.2063 StartZ=0 EndX=-12.3371 EndY=-29.2115 EndZ=0
    g268: LineSegment StartX=-12.3371 StartY=-29.2115 StartZ=0 EndX=-12.6214 EndY=-29.2769 EndZ=0
    g269: LineSegment StartX=-12.6214 StartY=-29.2769 StartZ=0 EndX=-12.7965 EndY=-29.3241 EndZ=0
    g270: LineSegment StartX=-12.7965 StartY=-29.3241 StartZ=0 EndX=-12.9198 EndY=-29.399 EndZ=0
    g271: LineSegment StartX=-12.9198 StartY=-29.399 StartZ=0 EndX=-13.3979 EndY=-29.7132 EndZ=0
    g272: LineSegment StartX=-13.3979 StartY=-29.7132 StartZ=0 EndX=-13.4863 EndY=-29.8176 EndZ=0
    g273: LineSegment StartX=-13.4863 StartY=-29.8176 StartZ=0 EndX=-13.546 EndY=-29.8853 EndZ=0
    g274: LineSegment StartX=-13.546 StartY=-29.8853 StartZ=0 EndX=-13.7573 EndY=-30.2176 EndZ=0
    g275: LineSegment StartX=-13.7573 StartY=-30.2176 StartZ=0 EndX=-13.8384 EndY=-30.3835 EndZ=0
    g276: LineSegment StartX=-13.8384 StartY=-30.3835 StartZ=0 EndX=-13.8859 EndY=-30.656 EndZ=0
    g277: LineSegment StartX=-13.8859 StartY=-30.656 StartZ=0 EndX=-13.9468 EndY=-30.9444 EndZ=0
    g278: LineSegment StartX=-13.9468 StartY=-30.9444 StartZ=0 EndX=-13.9327 EndY=-31.1371 EndZ=0
    g279: LineSegment StartX=-13.9327 StartY=-31.1371 StartZ=0 EndX=-13.9022 EndY=-31.4101 EndZ=0
    g280: LineSegment StartX=-13.9022 StartY=-31.4101 StartZ=0 EndX=-13.799 EndY=-31.6893 EndZ=0
    g281: LineSegment StartX=-13.799 StartY=-31.6893 StartZ=0 EndX=-13.7255 EndY=-31.8642 EndZ=0
    g282: LineSegment StartX=-13.7255 StartY=-31.8642 StartZ=0 EndX=-13.6717 EndY=-31.9318 EndZ=0
    g283: LineSegment StartX=-13.6717 StartY=-31.9318 StartZ=0 EndX=-13.4983 EndY=-32.1276 EndZ=0
    g284: LineSegment StartX=-13.4983 StartY=-32.1276 StartZ=0 EndX=-13.2463 EndY=-32.4223 EndZ=0
    g285: LineSegment StartX=-13.2463 StartY=-32.4223 StartZ=0 EndX=-12.9993 EndY=-32.5497 EndZ=0
    g286: LineSegment StartX=-12.9993 StartY=-32.5497 StartZ=0 EndX=-12.7377 EndY=-32.6968 EndZ=0
    g287: LineSegment StartX=-12.7377 StartY=-32.6968 StartZ=0 EndX=-12.6901 EndY=-32.7078 EndZ=0
    g288: LineSegment StartX=-40.0114 StartY=-32.7304 StartZ=0 EndX=-39.8799 EndY=-32.7533 EndZ=0
    g289: LineSegment StartX=-39.8799 StartY=-32.7533 StartZ=0 EndX=-39.5842 EndY=-32.7948 EndZ=0
    g290: LineSegment StartX=-39.5842 StartY=-32.7948 StartZ=0 EndX=-39.1893 EndY=-32.7105 EndZ=0
    g291: LineSegment StartX=-39.1893 StartY=-32.7105 StartZ=0 EndX=-39.0201 EndY=-32.6701 EndZ=0
    g292: LineSegment StartX=-39.0201 StartY=-32.6701 StartZ=0 EndX=-38.9005 EndY=-32.6528 EndZ=0
    g293: LineSegment StartX=-38.9005 StartY=-32.6528 StartZ=0 EndX=-38.7189 EndY=-32.559 EndZ=0
    g294: LineSegment StartX=-38.7189 StartY=-32.559 StartZ=0 EndX=-38.4489 EndY=-32.3904 EndZ=0
    g295: LineSegment StartX=-38.4489 StartY=-32.3904 StartZ=0 EndX=-38.2311 EndY=-32.1462 EndZ=0
    g296: LineSegment StartX=-38.2311 StartY=-32.1462 StartZ=0 EndX=-38.0816 EndY=-31.9793 EndZ=0
    g297: LineSegment StartX=-38.0816 StartY=-31.9793 StartZ=0 EndX=-37.9491 EndY=-31.7013 EndZ=0
    g298: LineSegment StartX=-37.9491 StartY=-31.7013 StartZ=0 EndX=-37.8591 EndY=-31.4661 EndZ=0
    g299: LineSegment StartX=-37.8591 StartY=-31.4661 StartZ=0 EndX=-37.8241 EndY=-31.2187 EndZ=0
    g300: LineSegment StartX=-37.8241 StartY=-31.2187 StartZ=0 EndX=-37.7953 EndY=-31.0749 EndZ=0
    g301: LineSegment StartX=-37.7953 StartY=-31.0749 StartZ=0 EndX=-37.8121 EndY=-30.7392 EndZ=0
    g302: LineSegment StartX=-37.8121 StartY=-30.7392 StartZ=0 EndX=-37.8222 EndY=-30.6611 EndZ=0
    g303: LineSegment StartX=-37.8222 StartY=-30.6611 StartZ=0 EndX=-38.0392 EndY=-30.1036 EndZ=0
    g304: LineSegment StartX=-38.0392 StartY=-30.1036 StartZ=0 EndX=-38.0964 EndY=-29.9984 EndZ=0
    g305: LineSegment StartX=-38.0964 StartY=-29.9984 StartZ=0 EndX=-38.2596 EndY=-29.8002 EndZ=0
    g306: LineSegment StartX=-38.2596 StartY=-29.8002 StartZ=0 EndX=-38.4191 EndY=-29.6352 EndZ=0
    g307: LineSegment StartX=-38.4191 StartY=-29.6352 StartZ=0 EndX=-38.6679 EndY=-29.4705 EndZ=0
    g308: LineSegment StartX=-38.6679 StartY=-29.4705 StartZ=0 EndX=-38.7517 EndY=-29.4248 EndZ=0
    g309: LineSegment StartX=-38.7517 StartY=-29.4248 StartZ=0 EndX=-38.8713 EndY=-29.3598 EndZ=0
    g310: LineSegment StartX=-38.8713 StartY=-29.3598 StartZ=0 EndX=-38.9984 EndY=-29.316 EndZ=0
    g311: LineSegment StartX=-38.9984 StartY=-29.316 StartZ=0 EndX=-39.2891 EndY=-29.2273 EndZ=0
    g312: LineSegment StartX=-39.2891 StartY=-29.2273 StartZ=0 EndX=-39.6407 EndY=-29.2235 EndZ=0
    g313: LineSegment StartX=-39.6407 StartY=-29.2235 StartZ=0 EndX=-39.8474 EndY=-29.2269 EndZ=0
    g314: LineSegment StartX=-39.8474 StartY=-29.2269 StartZ=0 EndX=-39.8557 EndY=-29.2278 EndZ=0
    g315: LineSegment StartX=-39.8557 StartY=-29.2278 StartZ=0 EndX=-39.9497 EndY=-29.2385 EndZ=0
    g316: LineSegment StartX=-39.9497 StartY=-29.2385 StartZ=0 EndX=-40.0586 EndY=-29.2655 EndZ=0
    g317: LineSegment StartX=-40.0586 StartY=-29.2655 StartZ=0 EndX=-40.187 EndY=-29.3068 EndZ=0
    g318: LineSegment StartX=-40.187 StartY=-29.3068 StartZ=0 EndX=-40.5712 EndY=-29.5122 EndZ=0
    g319: LineSegment StartX=-40.5712 StartY=-29.5122 StartZ=0 EndX=-40.6783 EndY=-29.5797 EndZ=0
    g320: LineSegment StartX=-40.6783 StartY=-29.5797 StartZ=0 EndX=-40.7385 EndY=-29.6488 EndZ=0
    g321: LineSegment StartX=-40.7385 StartY=-29.6488 StartZ=0 EndX=-41.1242 EndY=-30.0786 EndZ=0
    g322: LineSegment StartX=-41.1242 StartY=-30.0786 StartZ=0 EndX=-41.1757 EndY=-30.1894 EndZ=0
    g323: LineSegment StartX=-41.1757 StartY=-30.1894 StartZ=0 EndX=-41.2146 EndY=-30.267 EndZ=0
    g324: LineSegment StartX=-41.2146 StartY=-30.267 StartZ=0 EndX=-41.3308 EndY=-30.5585 EndZ=0
    g325: LineSegment StartX=-41.3308 StartY=-30.5585 StartZ=0 EndX=-41.3646 EndY=-30.8117 EndZ=0
    g326: LineSegment StartX=-41.3646 StartY=-30.8117 StartZ=0 EndX=-41.3838 EndY=-31.0017 EndZ=0
    g327: LineSegment StartX=-41.3838 StartY=-31.0017 StartZ=0 EndX=-41.3625 EndY=-31.2044 EndZ=0
    g328: LineSegment StartX=-41.3625 StartY=-31.2044 StartZ=0 EndX=-41.3237 EndY=-31.4664 EndZ=0
    g329: LineSegment StartX=-41.3237 StartY=-31.4664 StartZ=0 EndX=-41.2119 EndY=-31.7441 EndZ=0
    g330: LineSegment StartX=-41.2119 StartY=-31.7441 StartZ=0 EndX=-41.174 EndY=-31.8179 EndZ=0
    g331: LineSegment StartX=-41.174 StartY=-31.8179 StartZ=0 EndX=-41.0427 EndY=-32.0361 EndZ=0
    g332: LineSegment StartX=-41.0427 StartY=-32.0361 StartZ=0 EndX=-40.7723 EndY=-32.3362 EndZ=0
    g333: LineSegment StartX=-40.7723 StartY=-32.3362 StartZ=0 EndX=-40.7082 EndY=-32.3883 EndZ=0
    g334: LineSegment StartX=-40.7082 StartY=-32.3883 StartZ=0 EndX=-40.6107 EndY=-32.4705 EndZ=0
    g335: LineSegment StartX=-40.6107 StartY=-32.4705 StartZ=0 EndX=-40.5005 EndY=-32.5342 EndZ=0
    g336: LineSegment StartX=-40.5005 StartY=-32.5342 StartZ=0 EndX=-40.227 EndY=-32.6802 EndZ=0
    g337: LineSegment StartX=-40.227 StartY=-32.6802 StartZ=0 EndX=-40.1443 EndY=-32.7122 EndZ=0
    g338: LineSegment StartX=-40.1443 StartY=-32.7122 StartZ=0 EndX=-40.0114 EndY=-32.7304 EndZ=0
    g339: LineSegment StartX=-62.2472 StartY=-6.15472 StartZ=0 EndX=-62.1549 EndY=-6.10598 EndZ=0
    g340: LineSegment StartX=-62.1549 StartY=-6.10598 StartZ=0 EndX=-61.944 EndY=-5.95982 EndZ=0
    g341: LineSegment StartX=-61.944 StartY=-5.95982 StartZ=0 EndX=-61.8112 EndY=-5.85654 EndZ=0
    g342: LineSegment StartX=-61.8112 StartY=-5.85654 StartZ=0 EndX=-61.7303 EndY=-5.77383 EndZ=0
    g343: LineSegment StartX=-61.7303 StartY=-5.77383 StartZ=0 EndX=-61.7234 EndY=-5.76681 EndZ=0
    g344: LineSegment StartX=-61.7234 StartY=-5.76681 StartZ=0 EndX=-61.6512 EndY=-5.69063 EndZ=0
    g345: LineSegment StartX=-61.6512 StartY=-5.69063 StartZ=0 EndX=-61.479 EndY=-5.47716 EndZ=0
    g346: LineSegment StartX=-61.479 StartY=-5.47716 StartZ=0 EndX=-61.359 EndY=-5.21728 EndZ=0
    g347: LineSegment StartX=-61.359 StartY=-5.21728 StartZ=0 EndX=-61.3197 EndY=-5.10625 EndZ=0
    g348: LineSegment StartX=-61.3197 StartY=-5.10625 StartZ=0 EndX=-61.2657 EndY=-4.9677 EndZ=0
    g349: LineSegment StartX=-61.2657 StartY=-4.9677 StartZ=0 EndX=-61.2297 EndY=-4.70575 EndZ=0
    g350: LineSegment StartX=-61.2297 StartY=-4.70575 StartZ=0 EndX=-61.2 EndY=-4.52 EndZ=0
    g351: LineSegment StartX=-61.2 StartY=-4.52 StartZ=0 EndX=-61.2514 EndY=-4.11083 EndZ=0
    g352: LineSegment StartX=-61.2514 StartY=-4.11083 StartZ=0 EndX=-61.255 EndY=-4.07864 EndZ=0
    g353: LineSegment StartX=-61.255 StartY=-4.07864 StartZ=0 EndX=-61.257 EndY=-4.07309 EndZ=0
    g354: LineSegment StartX=-61.257 StartY=-4.07309 StartZ=0 EndX=-61.2622 EndY=-4.05849 EndZ=0
    g355: LineSegment StartX=-61.2622 StartY=-4.05849 StartZ=0 EndX=-61.5075 EndY=-3.54445 EndZ=0
    g356: LineSegment StartX=-61.5075 StartY=-3.54445 StartZ=0 EndX=-61.5191 EndY=-3.5202 EndZ=0
    g357: LineSegment StartX=-61.5191 StartY=-3.5202 StartZ=0 EndX=-61.5488 EndY=-3.46604 EndZ=0
    g358: LineSegment StartX=-61.5488 StartY=-3.46604 StartZ=0 EndX=-61.7455 EndY=-3.27754 EndZ=0
    g359: LineSegment StartX=-61.7455 StartY=-3.27754 StartZ=0 EndX=-61.9473 EndY=-3.06577 EndZ=0
    g360: LineSegment StartX=-61.9473 StartY=-3.06577 StartZ=0 EndX=-62.1054 EndY=-2.97369 EndZ=0
    g361: LineSegment StartX=-62.1054 StartY=-2.97369 StartZ=0 EndX=-62.4974 EndY=-2.80039 EndZ=0
    g362: LineSegment StartX=-62.4974 StartY=-2.80039 StartZ=0 EndX=-62.5245 EndY=-2.78653 EndZ=0
    g363: LineSegment StartX=-62.5245 StartY=-2.78653 StartZ=0 EndX=-62.525 EndY=-2.78641 EndZ=0
    g364: LineSegment StartX=-62.525 StartY=-2.78641 StartZ=0 EndX=-62.5321 EndY=-2.7844 EndZ=0
    g365: LineSegment StartX=-62.5321 StartY=-2.7844 StartZ=0 EndX=-62.5348 EndY=-2.78401 EndZ=0
    g366: LineSegment StartX=-62.5348 StartY=-2.78401 StartZ=0 EndX=-62.9194 EndY=-2.729 EndZ=0
    g367: LineSegment StartX=-62.9194 StartY=-2.729 StartZ=0 EndX=-63.1399 EndY=-2.72975 EndZ=0
    g368: LineSegment StartX=-63.1399 StartY=-2.72975 StartZ=0 EndX=-63.2829 EndY=-2.74951 EndZ=0
    g369: LineSegment StartX=-63.2829 StartY=-2.74951 StartZ=0 EndX=-63.4555 EndY=-2.80043 EndZ=0
    g370: LineSegment StartX=-63.4555 StartY=-2.80043 StartZ=0 EndX=-63.7254 EndY=-2.87771 EndZ=0
    g371: LineSegment StartX=-63.7254 StartY=-2.87771 StartZ=0 EndX=-63.8821 EndY=-2.96868 EndZ=0
    g372: LineSegment StartX=-63.8821 StartY=-2.96868 StartZ=0 EndX=-64.2139 EndY=-3.21019 EndZ=0
    g373: LineSegment StartX=-64.2139 StartY=-3.21019 StartZ=0 EndX=-64.3028 EndY=-3.29074 EndZ=0
    g374: LineSegment StartX=-64.3028 StartY=-3.29074 StartZ=0 EndX=-64.377 EndY=-3.38533 EndZ=0
    g375: LineSegment StartX=-64.377 StartY=-3.38533 StartZ=0 EndX=-64.6679 EndY=-3.88611 EndZ=0
    g376: LineSegment StartX=-64.6679 StartY=-3.88611 StartZ=0 EndX=-64.7038 EndY=-3.95543 EndZ=0
    g377: LineSegment StartX=-64.7038 StartY=-3.95543 StartZ=0 EndX=-64.7407 EndY=-4.20315 EndZ=0
    g378: LineSegment StartX=-64.7407 StartY=-4.20315 StartZ=0 EndX=-64.7957 EndY=-4.51157 EndZ=0
    g379: LineSegment StartX=-64.7957 StartY=-4.51157 StartZ=0 EndX=-64.7752 EndY=-4.71996 EndZ=0
    g380: LineSegment StartX=-64.7752 StartY=-4.71996 StartZ=0 EndX=-64.743 EndY=-4.95931 EndZ=0
    g381: LineSegment StartX=-64.743 StartY=-4.95931 StartZ=0 EndX=-64.626 EndY=-5.2564 EndZ=0
    g382: LineSegment StartX=-64.626 StartY=-5.2564 StartZ=0 EndX=-64.5891 EndY=-5.33083 EndZ=0
    g383: LineSegment StartX=-64.5891 StartY=-5.33083 StartZ=0 EndX=-64.5375 EndY=-5.43891 EndZ=0
    g384: LineSegment StartX=-64.5375 StartY=-5.43891 StartZ=0 EndX=-64.4817 EndY=-5.50296 EndZ=0
    g385: LineSegment StartX=-64.4817 StartY=-5.50296 StartZ=0 EndX=-64.2167 EndY=-5.84657 EndZ=0
    g386: LineSegment StartX=-64.2167 StartY=-5.84657 StartZ=0 EndX=-63.9946 EndY=-6.0154 EndZ=0
    g387: LineSegment StartX=-63.9946 StartY=-6.0154 StartZ=0 EndX=-63.986 EndY=-6.02173 EndZ=0
    g388: LineSegment StartX=-63.986 StartY=-6.02173 StartZ=0 EndX=-63.9774 EndY=-6.02755 EndZ=0
    g389: LineSegment StartX=-63.9774 StartY=-6.02755 StartZ=0 EndX=-63.6386 EndY=-6.19941 EndZ=0
    g390: LineSegment StartX=-63.6386 StartY=-6.19941 StartZ=0 EndX=-63.6285 EndY=-6.20188 EndZ=0
    g391: LineSegment StartX=-63.6285 StartY=-6.20188 StartZ=0 EndX=-63.3122 EndY=-6.28808 EndZ=0
    g392: LineSegment StartX=-63.3122 StartY=-6.28808 StartZ=0 EndX=-63.041 EndY=-6.31527 EndZ=0
    g393: LineSegment StartX=-63.041 StartY=-6.31527 StartZ=0 EndX=-62.8908 EndY=-6.31418 EndZ=0
    g394: LineSegment StartX=-62.8908 StartY=-6.31418 StartZ=0 EndX=-62.546 EndY=-6.23828 EndZ=0
    g395: LineSegment StartX=-62.546 StartY=-6.23828 StartZ=0 EndX=-62.3502 EndY=-6.18946 EndZ=0
    g396: LineSegment StartX=-62.3502 StartY=-6.18946 StartZ=0 EndX=-62.2472 EndY=-6.15472 EndZ=0
    g397: LineSegment StartX=29.3184 StartY=-4.4128 StartZ=0 EndX=29.3441 EndY=-4.63425 EndZ=0
    g398: LineSegment StartX=29.3441 StartY=-4.63425 StartZ=0 EndX=29.3837 EndY=-5.02957 EndZ=0
    g399: LineSegment StartX=29.3837 StartY=-5.02957 StartZ=0 EndX=29.4459 EndY=-5.17119 EndZ=0
    ... +280 more geometry lines
  constraints (701):
    c: Coincident(g0,g1)
    c: Coincident(g1,g2)
    c: Coincident(g2,g3)
    c: Coincident(g3,g4)
    c: Vertical(g4)
    c: Coincident(g4,g5)
    c: Horizontal(g5)
    c: Coincident(g5,g6)
    c: Coincident(g6,g7)
    c: Coincident(g7,g8)
    c: Coincident(g8,g9)
    c: Coincident(g9,g10)
    c: Coincident(g10,g11)
    c: Coincident(g11,g12)
    c: Coincident(g12,g13)
    c: Coincident(g13,g14)
    c: Coincident(g14,g15)
    c: Coincident(g15,g16)
    c: Coincident(g16,g17)
    c: Coincident(g17,g18)
    c: Coincident(g18,g19)
    c: Coincident(g19,g20)
    c: Coincident(g20,g21)
    c: Coincident(g21,g22)
    c: Coincident(g22,g23)
    c: Coincident(g23,g24)
    c: Coincident(g24,g25)
    c: Coincident(g25,g26)
    c: Coincident(g26,g27)
    c: Coincident(g27,g28)
    c: Coincident(g28,g29)
    c: Coincident(g29,g30)
    c: Coincident(g30,g31)
    c: Horizontal(g31)
    c: Coincident(g31,g32)
    c: Vertical(g32)
    c: Coincident(g32,g33)
    c: Horizontal(g33)
    c: Coincident(g33,g34)
    c: Vertical(g34)
    c: Coincident(g34,g35)
    c: Horizontal(g35)
    c: Coincident(g35,g36)
    c: Vertical(g36)
    c: Coincident(g36,g37)
    c: Horizontal(g37)
    c: Coincident(g37,g38)
    c: Vertical(g38)
    c: Coincident(g38,g39)
    c: Horizontal(g39)
    c: Coincident(g39,g40)
    c: Vertical(g40)
    c: Coincident(g40,g41)
    c: Horizontal(g41)
    c: Coincident(g41,g42)
    c: Vertical(g42)
    c: Coincident(g42,g43)
    c: Horizontal(g43)
    c: Coincident(g43,g44)
    c: Vertical(g44)
    c: Coincident(g44,g45)
    c: Coincident(g45,g46)
    c: Coincident(g46,g47)
    c: Coincident(g47,g48)
    c: Coincident(g48,g49)
    c: Coincident(g49,g50)
    c: Coincident(g50,g51)
    c: Coincident(g51,g52)
    c: Coincident(g52,g53)
    c: Coincident(g53,g54)
    c: Coincident(g54,g55)
    c: Coincident(g55,g56)
    c: Coincident(g56,g57)
    c: Coincident(g57,g58)
    c: Coincident(g58,g59)
    c: Coincident(g59,g60)
    c: Coincident(g60,g61)
    c: Coincident(g61,g62)
    c: Coincident(g62,g63)
    c: Coincident(g63,g64)
    c: Coincident(g64,g65)
    c: Coincident(g65,g66)
    c: Coincident(g66,g67)
    c: Coincident(g67,g68)
    c: Coincident(g68,g69)
    c: Coincident(g69,g70)
    c: Coincident(g70,g71)
    c: Coincident(g71,g72)
    c: Coincident(g72,g73)
    c: Coincident(g73,g74)
    c: Coincident(g74,g75)
    c: Coincident(g75,g76)
    c: Coincident(g76,g77)
    c: Horizontal(g77)
    c: Coincident(g77,g78)
    c: Coincident(g78,g79)
    c: Coincident(g79,g80)
    c: Coincident(g80,g81)
    c: Coincident(g81,g82)
    c: Coincident(g82,g83)
    c: Coincident(g83,g84)
    c: Coincident(g84,g85)
    c: Coincident(g85,g86)
    c: Coincident(g86,g87)
    c: Coincident(g87,g88)
    c: Coincident(g88,g89)
    c: Coincident(g89,g90)
    c: Coincident(g90,g91)
    c: Coincident(g91,g92)
    c: Coincident(g92,g93)
    c: Coincident(g93,g94)
    c: Coincident(g94,g95)
    c: Coincident(g95,g96)
    c: Coincident(g96,g97)
    c: Coincident(g97,g98)
    c: Coincident(g98,g99)
    c: Coincident(g99,g100)
    c: Coincident(g100,g101)
    c: Coincident(g101,g102)
    c: Coincident(g102,g103)
    c: Coincident(g103,g104)
    c: Coincident(g104,g105)
    c: Vertical(g105)
    c: Coincident(g105,g106)
    c: Horizontal(g106)
    c: Coincident(g106,g107)
    c: Vertical(g107)
    c: Coincident(g107,g108)
    c: Horizontal(g108)
    c: Coincident(g108,g109)
    c: Coincident(g109,g110)
    c: Coincident(g110,g111)
    c: Coincident(g111,g112)
    c: Coincident(g112,g113)
    c: Coincident(g113,g114)
    c: Coincident(g114,g115)
    c: Coincident(g115,g116)
    c: Coincident(g116,g117)
    c: Coincident(g117,g118)
    c: Coincident(g118,g119)
    c: Coincident(g119,g120)
    c: Coincident(g120,g121)
    c: Coincident(g121,g122)
    c: Coincident(g122,g123)
    c: Coincident(g123,g124)
    c: Coincident(g124,g125)
    c: Coincident(g125,g126)
    c: Coincident(g126,g127)
    c: Coincident(g127,g128)
    c: Coincident(g128,g0)
    c: Coincident(g129,g130)
    c: Coincident(g130,g131)
    c: Coincident(g131,g132)
    c: Coincident(g132,g133)
    c: Coincident(g133,g134)
    c: Coincident(g134,g135)
    c: Coincident(g135,g136)
    c: Coincident(g136,g137)
    c: Coincident(g137,g138)
    c: Coincident(g138,g139)
    c: Coincident(g139,g140)
    c: Coincident(g140,g141)
    c: Coincident(g141,g142)
    c: Coincident(g142,g143)
    c: Coincident(g143,g144)
    c: Coincident(g144,g145)
    c: Coincident(g145,g146)
    c: Coincident(g146,g147)
    c: Coincident(g147,g148)
    c: Coincident(g148,g149)
    c: Coincident(g149,g150)
    c: Coincident(g150,g151)
    c: Coincident(g151,g152)
    c: Coincident(g152,g153)
    c: Coincident(g153,g154)
    c: Coincident(g154,g155)
    c: Coincident(g155,g156)
    c: Coincident(g156,g157)
    c: Coincident(g157,g158)
    c: Coincident(g158,g159)
    c: Coincident(g159,g160)
    c: Coincident(g160,g161)
    c: Coincident(g161,g162)
    c: Coincident(g162,g163)
    c: Coincident(g163,g164)
    c: Coincident(g164,g165)
    c: Coincident(g165,g166)
    c: Coincident(g166,g167)
    c: Coincident(g167,g168)
    c: Coincident(g168,g169)
    c: Coincident(g169,g170)
    c: Coincident(g170,g171)
    c: Coincident(g171,g172)
    c: Coincident(g172,g173)
    c: Coincident(g173,g174)
    c: Coincident(g174,g175)
    c: Coincident(g175,g176)
    c: Coincident(g176,g177)
    c: Coincident(g177,g129)
    c: Coincident(g178,g179)
    c: Coincident(g179,g180)
    c: Coincident(g180,g181)
    c: Coincident(g181,g182)
    c: Coincident(g182,g183)
    c: Coincident(g183,g184)
    c: Coincident(g184,g185)
    c: Coincident(g185,g186)
    c: Coincident(g186,g187)
    c: Coincident(g187,g188)
    c: Coincident(g188,g189)
    c: Coincident(g189,g190)
    c: Coincident(g190,g191)
    c: Coincident(g191,g192)
    c: Coincident(g192,g193)
    c: Coincident(g193,g194)
    c: Coincident(g194,g195)
    c: Coincident(g195,g196)
    c: Coincident(g196,g197)
    c: Coincident(g197,g198)
    c: Coincident(g198,g199)
    c: Coincident(g199,g200)
    c: Coincident(g200,g201)
    c: Coincident(g201,g202)
    c: Coincident(g202,g203)
    c: Coincident(g203,g204)
    c: Coincident(g204,g205)
    c: Coincident(g205,g206)
    c: Coincident(g206,g207)
    c: Coincident(g207,g208)
    c: Coincident(g208,g209)
    c: Coincident(g209,g210)
    c: Coincident(g210,g211)
    c: Coincident(g211,g212)
    c: Coincident(g212,g213)
    c: Coincident(g213,g214)
    c: Coincident(g214,g215)
    c: Coincident(g215,g216)
    c: Coincident(g216,g217)
    c: Coincident(g217,g218)
    c: Coincident(g218,g219)
    c: Coincident(g219,g220)
    c: Coincident(g220,g221)
    c: Coincident(g221,g222)
    c: Coincident(g222,g223)
    c: Coincident(g223,g224)
    c: Coincident(g224,g225)
    c: Coincident(g225,g226)
    c: Coincident(g226,g227)
    c: Coincident(g227,g228)
    c: Coincident(g228,g229)
    c: Coincident(g229,g230)
    c: Coincident(g230,g231)
    c: Coincident(g231,g232)
    c: Coincident(g232,g233)
    c: Coincident(g233,g178)
    c: Coincident(g234,g235)
    c: Coincident(g235,g236)
    c: Coincident(g236,g237)
    c: Coincident(g237,g238)
    c: Coincident(g238,g239)
    c: Coincident(g239,g240)
    c: Coincident(g240,g241)
    c: Coincident(g241,g242)
    c: Coincident(g242,g243)
    c: Coincident(g243,g244)
    c: Coincident(g244,g245)
    c: Coincident(g245,g246)
    c: Coincident(g246,g247)
    c: Coincident(g247,g248)
    c: Coincident(g248,g249)
    c: Coincident(g249,g250)
    c: Coincident(g250,g251)
    c: Coincident(g251,g252)
    c: Coincident(g252,g253)
    c: Coincident(g253,g254)
    c: Coincident(g254,g255)
    c: Coincident(g255,g256)
    c: Coincident(g256,g257)
    c: Coincident(g257,g258)
    c: Coincident(g258,g259)
    c: Coincident(g259,g260)
    c: Coincident(g260,g261)
    c: Coincident(g261,g262)
    c: Coincident(g262,g263)
    c: Coincident(g263,g264)
    c: Coincident(g264,g265)
    c: Coincident(g265,g266)
    c: Coincident(g266,g267)
    c: Coincident(g267,g268)
    c: Coincident(g268,g269)
    c: Coincident(g269,g270)
    c: Coincident(g270,g271)
    c: Coincident(g271,g272)
    c: Coincident(g272,g273)
    c: Coincident(g273,g274)
    c: Coincident(g274,g275)
    c: Coincident(g275,g276)
    c: Coincident(g276,g277)
    c: Coincident(g277,g278)
    c: Coincident(g278,g279)
    c: Coincident(g279,g280)
    c: Coincident(g280,g281)
    c: Coincident(g281,g282)
    c: Coincident(g282,g283)
    c: Coincident(g283,g284)
    c: Coincident(g284,g285)
    c: Coincident(g285,g286)
    c: Coincident(g286,g287)
    c: Coincident(g287,g234)
    c: Coincident(g288,g289)
    c: Coincident(g289,g290)
    c: Coincident(g290,g291)
    c: Coincident(g291,g292)
    c: Coincident(g292,g293)
    c: Coincident(g293,g294)
    c: Coincident(g294,g295)
    c: Coincident(g295,g296)
    c: Coincident(g296,g297)
    c: Coincident(g297,g298)
    c: Coincident(g298,g299)
    c: Coincident(g299,g300)
    c: Coincident(g300,g301)
    c: Coincident(g301,g302)
    c: Coincident(g302,g303)
    c: Coincident(g303,g304)
    c: Coincident(g304,g305)
    c: Coincident(g305,g306)
    c: Coincident(g306,g307)
    c: Coincident(g307,g308)
    c: Coincident(g308,g309)
    c: Coincident(g309,g310)
    c: Coincident(g310,g311)
    c: Coincident(g311,g312)
    c: Coincident(g312,g313)
    c: Coincident(g313,g314)
    c: Coincident(g314,g315)
    c: Coincident(g315,g316)
    c: Coincident(g316,g317)
    c: Coincident(g317,g318)
    c: Coincident(g318,g319)
    c: Coincident(g319,g320)
    c: Coincident(g320,g321)
    c: Coincident(g321,g322)
    c: Coincident(g322,g323)
    c: Coincident(g323,g324)
    c: Coincident(g324,g325)
    c: Coincident(g325,g326)
    c: Coincident(g326,g327)
    c: Coincident(g327,g328)
    c: Coincident(g328,g329)
    c: Coincident(g329,g330)
    c: Coincident(g330,g331)
    c: Coincident(g331,g332)
    c: Coincident(g332,g333)
    c: Coincident(g333,g334)
    c: Coincident(g334,g335)
    c: Coincident(g335,g336)
    c: Coincident(g336,g337)
    c: Coincident(g337,g338)
    c: Coincident(g338,g288)
    c: Coincident(g339,g340)
    c: Coincident(g340,g341)
    c: Coincident(g341,g342)
    c: Coincident(g342,g343)
    c: Coincident(g343,g344)
    c: Coincident(g344,g345)
    c: Coincident(g345,g346)
    c: Coincident(g346,g347)
    c: Coincident(g347,g348)
    c: Coincident(g348,g349)
    c: Coincident(g349,g350)
    c: Coincident(g350,g351)
    c: Coincident(g351,g352)
    c: Coincident(g352,g353)
    c: Coincident(g353,g354)
    c: Coincident(g354,g355)
    c: Coincident(g355,g356)
    c: Coincident(g356,g357)
    c: Coincident(g357,g358)
    c: Coincident(g358,g359)
    c: Coincident(g359,g360)
    c: Coincident(g360,g361)
    c: Coincident(g361,g362)
    c: Coincident(g362,g363)
    c: Coincident(g363,g364)
    c: Coincident(g364,g365)
    c: Coincident(g365,g366)
    c: Coincident(g366,g367)
    c: Coincident(g367,g368)
    c: Coincident(g368,g369)
    c: Coincident(g369,g370)
    c: Coincident(g370,g371)
    c: Coincident(g371,g372)
    c: Coincident(g372,g373)
    c: Coincident(g373,g374)
    c: Coincident(g374,g375)
    c: Coincident(g375,g376)
    c: Coincident(g376,g377)
    c: Coincident(g377,g378)
    c: Coincident(g378,g379)
    c: Coincident(g379,g380)
    c: Coincident(g380,g381)
    c: Coincident(g381,g382)
    c: Coincident(g382,g383)
    c: Coincident(g383,g384)
    c: Coincident(g384,g385)
    c: Coincident(g385,g386)
    c: Coincident(g386,g387)
    c: Coincident(g387,g388)
    c: Coincident(g388,g389)
    c: Coincident(g389,g390)
    c: Coincident(g390,g391)
    c: Coincident(g391,g392)
    c: Coincident(g392,g393)
    c: Coincident(g393,g394)
    c: Coincident(g394,g395)
    c: Coincident(g395,g396)
    c: Coincident(g396,g339)
    c: Coincident(g397,g398)
    c: Coincident(g398,g399)
    c: Coincident(g399,g400)
    c: Coincident(g400,g401)
    c: Coincident(g401,g402)
    c: Coincident(g402,g403)
    c: Coincident(g403,g404)
    c: Coincident(g404,g405)
    c: Coincident(g405,g406)
    c: Coincident(g406,g407)
    c: Coincident(g407,g408)
    c: Coincident(g408,g409)
    c: Coincident(g409,g410)
    c: Coincident(g410,g411)
    c: Coincident(g411,g412)
    c: Coincident(g412,g413)
    c: Coincident(g413,g414)
    c: Coincident(g414,g415)
    c: Coincident(g415,g416)
    c: Coincident(g416,g417)
    c: Coincident(g417,g418)
    c: Coincident(g418,g419)
    c: Coincident(g419,g420)
    c: Coincident(g420,g421)
    c: Coincident(g421,g422)
    c: Coincident(g422,g423)
    c: Coincident(g423,g424)
    c: Coincident(g424,g425)
    c: Coincident(g425,g426)
    c: Coincident(g426,g427)
    c: Coincident(g427,g428)
    c: Coincident(g428,g429)
    c: Coincident(g429,g430)
    c: Coincident(g430,g431)
    c: Coincident(g431,g432)
    c: Coincident(g432,g433)
    c: Coincident(g433,g434)
    c: Coincident(g434,g435)
    c: Coincident(g435,g436)
    c: Coincident(g436,g437)
    c: Coincident(g437,g438)
    c: Coincident(g438,g439)
    c: Coincident(g439,g440)
    c: Coincident(g440,g441)
    c: Coincident(g441,g442)
    c: Coincident(g442,g443)
    c: Coincident(g443,g444)
    c: Coincident(g444,g445)
    c: Coincident(g445,g446)
    c: Coincident(g446,g447)
    c: Coincident(g447,g448)
    c: Coincident(g448,g449)
    c: Coincident(g449,g450)
    c: Coincident(g450,g451)
    c: Coincident(g451,g397)
    c: Coincident(g452,g453)
    c: Coincident(g453,g454)
    c: Coincident(g454,g455)
    c: Coincident(g455,g456)
    c: Coincident(g456,g457)
    c: Coincident(g457,g458)
    c: Coincident(g458,g459)
    c: Coincident(g459,g460)
    c: Coincident(g460,g461)
    c: Coincident(g461,g462)
    c: Coincident(g462,g463)
    c: Coincident(g463,g464)
    c: Coincident(g464,g465)
    c: Coincident(g465,g466)
    c: Coincident(g466,g467)
    c: Coincident(g467,g468)
    c: Coincident(g468,g469)
    c: Coincident(g469,g470)
    c: Coincident(g470,g471)
    c: Coincident(g471,g472)
    c: Coincident(g472,g473)
    c: Coincident(g473,g474)
    c: Coincident(g474,g475)
    c: Coincident(g475,g476)
    c: Coincident(g476,g477)
    c: Coincident(g477,g478)
    c: Coincident(g478,g479)
    c: Coincident(g479,g480)
    c: Coincident(g480,g481)
    c: Coincident(g481,g482)
    c: Coincident(g482,g483)
    c: Coincident(g483,g484)
    c: Coincident(g484,g485)
    c: Coincident(g485,g486)
    c: Coincident(g486,g487)
    c: Coincident(g487,g488)
    c: Coincident(g488,g489)
    c: Coincident(g489,g490)
    c: Coincident(g490,g491)
    c: Coincident(g491,g492)
    c: Coincident(g492,g493)
    c: Coincident(g493,g494)
    c: Coincident(g494,g495)
    c: Coincident(g495,g496)
    c: Coincident(g496,g497)
    c: Coincident(g497,g498)
    c: Coincident(g498,g499)
    c: Coincident(g499,g500)
    c: Coincident(g500,g501)
    c: Coincident(g501,g502)
    c: Coincident(g502,g503)
    c: Coincident(g503,g504)
    c: Coincident(g504,g505)
    c: Coincident(g505,g506)
    c: Coincident(g506,g507)
    c: Coincident(g507,g508)
    c: Coincident(g508,g452)
    c: Coincident(g509,g510)
    c: Coincident(g510,g511)
    c: Coincident(g511,g512)
    c: Coincident(g512,g513)
    c: Coincident(g513,g514)
    c: Coincident(g514,g515)
    c: Coincident(g515,g516)
    c: Coincident(g516,g517)
    c: Coincident(g517,g518)
    c: Coincident(g518,g519)
    c: Coincident(g519,g520)
    c: Coincident(g520,g521)
    c: Coincident(g521,g522)
    c: Coincident(g522,g523)
    c: Coincident(g523,g524)
    c: Coincident(g524,g525)
    c: Coincident(g525,g526)
    c: Coincident(g526,g527)
    c: Coincident(g527,g528)
    c: Coincident(g528,g529)
    c: Coincident(g529,g530)
    c: Coincident(g530,g531)
    c: Coincident(g531,g532)
    c: Coincident(g532,g533)
    c: Coincident(g533,g534)
    c: Coincident(g534,g535)
    c: Coincident(g535,g536)
    c: Coincident(g536,g537)
    c: Coincident(g537,g538)
    c: Coincident(g538,g539)
    c: Coincident(g539,g540)
    c: Coincident(g540,g541)
    c: Coincident(g541,g542)
    c: Coincident(g542,g543)
    c: Coincident(g543,g544)
    c: Coincident(g544,g545)
    c: Coincident(g545,g546)
    c: Coincident(g546,g547)
    c: Coincident(g547,g548)
    c: Coincident(g548,g549)
    c: Coincident(g549,g550)
    c: Coincident(g550,g551)
    c: Coincident(g551,g552)
    c: Coincident(g552,g553)
    c: Coincident(g553,g554)
    c: Coincident(g554,g555)
    c: Coincident(g555,g556)
    c: Coincident(g556,g557)
    c: Coincident(g557,g558)
    c: Coincident(g558,g559)
    c: Coincident(g559,g560)
    c: Coincident(g560,g561)
    c: Coincident(g561,g562)
    c: Coincident(g562,g563)
    c: Coincident(g563,g564)
    c: Coincident(g564,g565)
    c: Coincident(g565,g566)
    c: Coincident(g566,g567)
    c: Coincident(g567,g568)
    c: Coincident(g568,g569)
    c: Coincident(g569,g509)
    c: Coincident(g570,g571)
    c: Coincident(g571,g572)
    c: Coincident(g572,g573)
    c: Coincident(g573,g574)
    c: Coincident(g574,g575)
    c: Coincident(g575,g576)
    c: Coincident(g576,g577)
    c: Coincident(g577,g578)
    c: Coincident(g578,g579)
    c: Coincident(g579,g580)
    c: Coincident(g580,g581)
    c: Coincident(g581,g582)
    c: Coincident(g582,g583)
    c: Coincident(g583,g584)
    c: Coincident(g584,g585)
    c: Coincident(g585,g586)
    c: Coincident(g586,g587)
    c: Coincident(g587,g588)
    c: Coincident(g588,g589)
    c: Coincident(g589,g590)
    c: Coincident(g590,g591)
    c: Coincident(g591,g592)
    c: Coincident(g592,g593)
    c: Coincident(g593,g594)
    c: Coincident(g594,g595)
    c: Coincident(g595,g596)
    c: Coincident(g596,g597)
    c: Coincident(g597,g598)
    c: Coincident(g598,g599)
    c: Coincident(g599,g600)
    c: Coincident(g600,g601)
    c: Coincident(g601,g602)
    c: Coincident(g602,g603)
    c: Coincident(g603,g604)
    c: Coincident(g604,g605)
    c: Coincident(g605,g606)
    c: Coincident(g606,g607)
    c: Coincident(g607,g608)
    c: Coincident(g608,g609)
    c: Coincident(g609,g610)
    c: Coincident(g610,g611)
    c: Coincident(g611,g612)
    c: Coincident(g612,g613)
    c: Coincident(g613,g614)
    c: Coincident(g614,g615)
    c: Coincident(g615,g616)
    c: Coincident(g616,g617)
    c: Coincident(g617,g618)
    c: Coincident(g618,g570)
    c: Coincident(g619,g620)
    c: Coincident(g620,g621)
    c: Coincident(g621,g622)
    c: Coincident(g622,g623)
    c: Coincident(g623,g624)
    c: Coincident(g624,g625)
    c: Coincident(g625,g626)
    c: Coincident(g626,g627)
    c: Coincident(g627,g628)
    c: Coincident(g628,g629)
    c: Coincident(g629,g630)
    c: Coincident(g630,g631)
    c: Coincident(g631,g632)
    c: Coincident(g632,g633)
    c: Coincident(g633,g634)
    c: Coincident(g634,g635)
    c: Coincident(g635,g636)
    c: Coincident(g636,g637)
    c: Coincident(g637,g638)
    c: Coincident(g638,g639)
    c: Coincident(g639,g640)
    c: Coincident(g640,g641)
    c: Coincident(g641,g642)
    c: Coincident(g642,g643)
    c: Coincident(g643,g644)
    c: Coincident(g644,g645)
    c: Coincident(g645,g646)
    c: Coincident(g646,g647)
    c: Coincident(g647,g648)
    c: Coincident(g648,g649)
    c: Coincident(g649,g650)
    c: Coincident(g650,g651)
    c: Coincident(g651,g652)
    c: Coincident(g652,g653)
    c: Coincident(g653,g654)
    c: Coincident(g654,g655)
    c: Coincident(g655,g656)
    c: Coincident(g656,g657)
    c: Coincident(g657,g658)
    c: Coincident(g658,g659)
    c: Coincident(g659,g660)
    c: Coincident(g660,g661)
    c: Coincident(g661,g662)
    c: Coincident(g662,g663)
    c: Coincident(g663,g664)
    c: Coincident(g664,g665)
    c: Coincident(g665,g666)
    c: Coincident(g666,g667)
    c: Coincident(g667,g668)
    c: Coincident(g668,g669)
    c: Coincident(g669,g670)
    c: Coincident(g670,g671)
    c: Coincident(g671,g672)
    c: Coincident(g672,g673)
    c: Coincident(g673,g674)
    c: Coincident(g674,g675)
    c: Coincident(g675,g676)
    c: Coincident(g676,g677)
    c: Coincident(g677,g678)
    c: Coincident(g678,g679)
    c: Coincident(g679,g619)
FEATURE [Mesh::Feature] Powerful_Habbi__1_  label="Powerful Habbi (1)"
FEATURE [Mesh::Feature] Powerful_Habbi__1_001  label="Powerful Habbi (1)001"
FEATURE [Part::Feature] Powerful_Habbi__1_001001
  shape: bbox 3.995 x 8.007 x 38 mm, 250 faces, 0 solids (baked)
FEATURE [Part::Refine] Powerful_Habbi__1_001001001
  Source = -> Powerful_Habbi__1_001001
FEATURE [Part::Feature] Powerful_Habbi__1_001001001_cs
  shape: bbox 3e-07 x 8.007 x 38 mm, 0 faces, 0 solids (baked)
FEATURE [Sketcher::SketchObject] Sketch006
  FullyConstrained = false
  Placement = pos=(0,0,0) rot=(0,1,0;1.5708rad)
  sketch-geometry (37):
    g0: LineSegment StartX=-66.6354 StartY=23.748 StartZ=0 EndX=-66.666 EndY=24.5328 EndZ=0
    g1: LineSegment StartX=-66.666 StartY=24.5328 StartZ=0 EndX=-66.6641 EndY=24.593 EndZ=0
    g2: LineSegment StartX=-66.6641 StartY=24.593 StartZ=0 EndX=-58.599 EndY=24.593 EndZ=0
    g3: LineSegment StartX=-58.599 StartY=24.593 StartZ=0 EndX=-58.599 EndY=21.991 EndZ=0
    g4: LineSegment StartX=-58.599 StartY=21.991 StartZ=0 EndX=-57.699 EndY=21.991 EndZ=0
    g5: LineSegment StartX=-57.699 StartY=21.991 StartZ=0 EndX=-57.699 EndY=24.593 EndZ=0
    g6: LineSegment StartX=-57.699 StartY=24.593 StartZ=0 EndX=-55.199 EndY=24.593 EndZ=0
    g7: LineSegment StartX=-55.199 StartY=24.593 StartZ=0 EndX=-55.199 EndY=19.589 EndZ=0
    g8: LineSegment StartX=-55.199 StartY=19.589 StartZ=0 EndX=-55.18 EndY=19.589 EndZ=0
    g9: LineSegment StartX=-55.18 StartY=19.589 StartZ=0 EndX=-55.18 EndY=17.787 EndZ=0
    g10: LineSegment StartX=-55.18 StartY=17.787 StartZ=0 EndX=-39.499 EndY=17.787 EndZ=0
    g11: LineSegment StartX=-39.499 StartY=17.787 StartZ=0 EndX=-39.499 EndY=24.593 EndZ=0
    g12: LineSegment StartX=-39.499 StartY=24.593 StartZ=0 EndX=-33.499 EndY=24.593 EndZ=0
    g13: LineSegment StartX=-33.499 StartY=24.593 StartZ=0 EndX=-33.499 EndY=20.59 EndZ=0
    g14: LineSegment StartX=-33.499 StartY=20.59 StartZ=0 EndX=-32.003 EndY=20.59 EndZ=0
    g15: LineSegment StartX=-32.003 StartY=20.59 StartZ=0 EndX=-32.003 EndY=16.586 EndZ=0
    g16: LineSegment StartX=-32.003 StartY=16.586 StartZ=0 EndX=-69.998 EndY=16.586 EndZ=0
    g17: LineSegment StartX=-69.998 StartY=16.586 StartZ=0 EndX=-69.998 EndY=24.593 EndZ=0
    g18: LineSegment StartX=-69.998 StartY=24.593 StartZ=0 EndX=-68.4192 EndY=24.593 EndZ=0
    g19: LineSegment StartX=-68.4192 StartY=24.593 StartZ=0 EndX=-68.4193 EndY=24.5884 EndZ=0
    g20: LineSegment StartX=-68.4193 StartY=24.5884 StartZ=0 EndX=-68.4212 EndY=24.5217 EndZ=0
    g21: LineSegment StartX=-68.4212 StartY=24.5217 StartZ=0 EndX=-68.3875 EndY=23.3934 EndZ=0
    g22: LineSegment StartX=-68.3875 StartY=23.3934 StartZ=0 EndX=-68.4127 EndY=22.4797 EndZ=0
    g23: LineSegment StartX=-68.4127 StartY=22.4797 StartZ=0 EndX=-68.3979 EndY=22.0958 EndZ=0
    g24: LineSegment StartX=-68.3979 StartY=22.0958 StartZ=0 EndX=-68.4105 EndY=21.7464 EndZ=0
    g25: LineSegment StartX=-68.4105 StartY=21.7464 StartZ=0 EndX=-68.3916 EndY=20.7371 EndZ=0
    g26: LineSegment StartX=-68.3916 StartY=20.7371 StartZ=0 EndX=-68.4177 EndY=19.7849 EndZ=0
    g27: LineSegment StartX=-68.4177 StartY=19.7849 StartZ=0 EndX=-68.4116 EndY=19.589 EndZ=0
    g28: LineSegment StartX=-68.4116 StartY=19.589 StartZ=0 EndX=-66.6486 EndY=19.589 EndZ=0
    g29: LineSegment StartX=-66.6486 StartY=19.589 StartZ=0 EndX=-66.6223 EndY=20.0117 EndZ=0
    g30: LineSegment StartX=-66.6223 StartY=20.0117 StartZ=0 EndX=-66.6037 EndY=20.3897 EndZ=0
    g31: LineSegment StartX=-66.6037 StartY=20.3897 StartZ=0 EndX=-66.6485 EndY=21.8553 EndZ=0
    g32: LineSegment StartX=-66.6485 StartY=21.8553 StartZ=0 EndX=-66.6435 EndY=22.0972 EndZ=0
    g33: LineSegment StartX=-66.6435 StartY=22.0972 StartZ=0 EndX=-66.6552 EndY=22.4526 EndZ=0
    g34: LineSegment StartX=-66.6552 StartY=22.4526 StartZ=0 EndX=-66.6174 EndY=22.8687 EndZ=0
    g35: LineSegment StartX=-66.6174 StartY=22.8687 StartZ=0 EndX=-66.649 EndY=23.3211 EndZ=0
    g36: LineSegment StartX=-66.649 StartY=23.3211 StartZ=0 EndX=-66.6354 EndY=23.748 EndZ=0
  constraints (55):
    c: Coincident(g0,g1)
    c: Coincident(g1,g2)
    c: Horizontal(g2)
    c: Coincident(g2,g3)
    c: Vertical(g3)
    c: Coincident(g3,g4)
    c: Horizontal(g4)
    c: Coincident(g4,g5)
    c: Vertical(g5)
    c: Coincident(g5,g6)
    c: Horizontal(g6)
    c: Coincident(g6,g7)
    c: Vertical(g7)
    c: Coincident(g7,g8)
    c: Horizontal(g8)
    c: Coincident(g8,g9)
    c: Vertical(g9)
    c: Coincident(g9,g10)
    c: Horizontal(g10)
    c: Coincident(g10,g11)
    c: Vertical(g11)
    c: Coincident(g11,g12)
    c: Horizontal(g12)
    c: Coincident(g12,g13)
    c: Vertical(g13)
    c: Coincident(g13,g14)
    c: Horizontal(g14)
    c: Coincident(g14,g15)
    c: Vertical(g15)
    c: Coincident(g15,g16)
    c: Horizontal(g16)
    c: Coincident(g16,g17)
    c: Vertical(g17)
    c: Coincident(g17,g18)
    c: Horizontal(g18)
    c: Coincident(g18,g19)
    c: Coincident(g19,g20)
    c: Coincident(g20,g21)
    c: Coincident(g21,g22)
    c: Coincident(g22,g23)
    c: Coincident(g23,g24)
    c: Coincident(g24,g25)
    c: Coincident(g25,g26)
    c: Coincident(g26,g27)
    c: Coincident(g27,g28)
    c: Horizontal(g28)
    c: Coincident(g28,g29)
    c: Coincident(g29,g30)
    c: Coincident(g30,g31)
    c: Coincident(g31,g32)
    c: Coincident(g32,g33)
    c: Coincident(g33,g34)
    c: Coincident(g34,g35)
    c: Coincident(g35,g36)
    c: Coincident(g36,g0)
